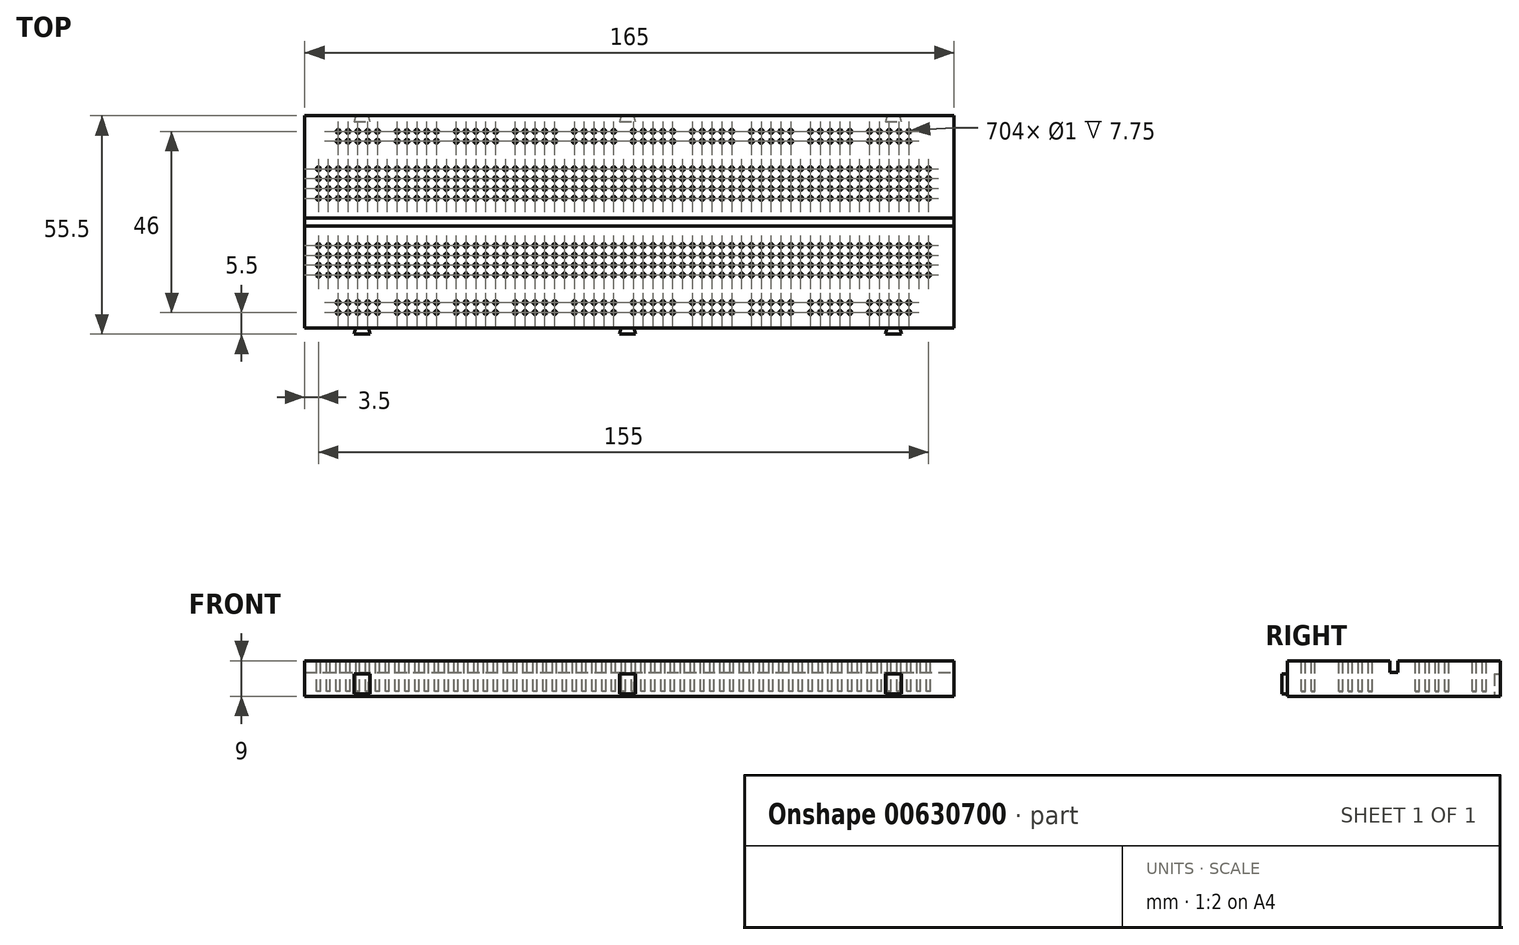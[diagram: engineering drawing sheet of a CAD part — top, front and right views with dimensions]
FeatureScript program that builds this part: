
annotation { "Feature Type Name" : "Feature", "Feature Type Description" : "" }
export const myFeature = defineFeature(function(context is Context, id is Id, definition is map)
    precondition{}
    {
        {
            var Q0;
            Q0=qCreatedBy(makeId("Top.planeOp"),FACE);
            var sketch = newSketch(context, id + "F0", { "sketchPlane" : qUnion([Q0])});
            skLineSegment(sketch, "E0.bottom", {"start": v(0, 0) * mm, "end": v(165, 0) * mm});
            skLineSegment(sketch, "E0.top", {"start": v(0, 54) * mm, "end": v(165, 54) * mm});
            skLineSegment(sketch, "E0.left", {"start": v(0, 0) * mm, "end": v(0, 54) * mm});
            skLineSegment(sketch, "E0.right", {"start": v(165, 0) * mm, "end": v(165, 54) * mm});
            skSolve(sketch);
        }
        {
            var Q0;
            Q0 = qSketchRegion(id + "F0", true);
            extrude(context, id + "F1", {"entities" : qUnion([Q0]), "depth" : 9 * mm, "offsetDistance" : 25 * mm});
        }
        {
            var Q0;
            Q0=makeQuery(id+"F1.opExtrude","CAP_FACE",FACE,{"disambiguationData":[OSD([sQuery(id+"F0.wireOp",EDGE,"E0.bottom"),sQuery(id+"F0.wireOp",EDGE,"E0.top"),sQuery(id+"F0.wireOp",EDGE,"E0.left"),sQuery(id+"F0.wireOp",EDGE,"E0.right")])],"isStart":false});
            var sketch = newSketch(context, id + "F2", { "sketchPlane" : qUnion([Q0])});
            skLineSegment(sketch, "E1.bottom", {"start": v(0, 28) * mm, "end": v(165, 28) * mm});
            skLineSegment(sketch, "E1.top", {"start": v(0, 26) * mm, "end": v(165, 26) * mm});
            skLineSegment(sketch, "E1.left", {"start": v(0, 28) * mm, "end": v(0, 26) * mm});
            skLineSegment(sketch, "E1.right", {"start": v(165, 28) * mm, "end": v(165, 26) * mm});
            skSolve(sketch);
        }
        {
            var Q0;
            Q0 = qSketchRegion(id + "F2", true);
            extrude(context, id + "F3", {"entities" : qUnion([Q0]), "operationType" : NewBodyOperationType.REMOVE, "oppositeDirection" : true, "depth" : 3 * mm, "offsetDistance" : 25 * mm});
        }
        {
            var Q0;
            {var subQ0=sQuery(id+"F0.wireOp",EDGE,"E0.top");var subQ1=sQuery(id+"F0.wireOp",EDGE,"E0.left");var subQ2=sQuery(id+"F0.wireOp",EDGE,"E0.right");Q0=makeQuery(id+"F3.boolean.opBoolean","SPLIT",FACE,{"disambiguationData":[TD([makeQuery(id+"F1.opExtrude","SWEPT_FACE",FACE,{"disambiguationData":[OSD([subQ0])]})])],"derivedFrom":makeQuery(id+"F1.opExtrude","CAP_FACE",FACE,{"disambiguationData":[OSD([sQuery(id+"F0.wireOp",EDGE,"E0.bottom"),subQ0,subQ1,subQ2])],"isStart":false})});}
            var sketch = newSketch(context, id + "F4", { "sketchPlane" : qUnion([Q0])});
            skCircle(sketch, "E2", {"center": v(3.5, 40.5) * mm, "radius": 0.5 * mm});
            skCircle(sketch, "E3", {"center": v(3.5, 38) * mm, "radius": 0.5 * mm});
            skCircle(sketch, "E4", {"center": v(3.5, 35.5) * mm, "radius": 0.5 * mm});
            skCircle(sketch, "E5", {"center": v(3.5, 33) * mm, "radius": 0.5 * mm});
            skCircle(sketch, "E6.1.0.0", {"center": v(6, 40.5) * mm, "radius": 0.5 * mm});
            skCircle(sketch, "E6.1.0.1", {"center": v(6, 38) * mm, "radius": 0.5 * mm});
            skCircle(sketch, "E6.1.0.2", {"center": v(6, 35.5) * mm, "radius": 0.5 * mm});
            skCircle(sketch, "E6.1.0.3", {"center": v(6, 33) * mm, "radius": 0.5 * mm});
            skCircle(sketch, "E6.2.0.0", {"center": v(8.5, 40.5) * mm, "radius": 0.5 * mm});
            skCircle(sketch, "E6.2.0.1", {"center": v(8.5, 38) * mm, "radius": 0.5 * mm});
            skCircle(sketch, "E6.2.0.2", {"center": v(8.5, 35.5) * mm, "radius": 0.5 * mm});
            skCircle(sketch, "E6.2.0.3", {"center": v(8.5, 33) * mm, "radius": 0.5 * mm});
            skCircle(sketch, "E6.3.0.0", {"center": v(11, 40.5) * mm, "radius": 0.5 * mm});
            skCircle(sketch, "E6.3.0.1", {"center": v(11, 38) * mm, "radius": 0.5 * mm});
            skCircle(sketch, "E6.3.0.2", {"center": v(11, 35.5) * mm, "radius": 0.5 * mm});
            skCircle(sketch, "E6.3.0.3", {"center": v(11, 33) * mm, "radius": 0.5 * mm});
            skCircle(sketch, "E6.4.0.0", {"center": v(13.5, 40.5) * mm, "radius": 0.5 * mm});
            skCircle(sketch, "E6.4.0.1", {"center": v(13.5, 38) * mm, "radius": 0.5 * mm});
            skCircle(sketch, "E6.4.0.2", {"center": v(13.5, 35.5) * mm, "radius": 0.5 * mm});
            skCircle(sketch, "E6.4.0.3", {"center": v(13.5, 33) * mm, "radius": 0.5 * mm});
            skCircle(sketch, "E6.5.0.0", {"center": v(16, 40.5) * mm, "radius": 0.5 * mm});
            skCircle(sketch, "E6.5.0.1", {"center": v(16, 38) * mm, "radius": 0.5 * mm});
            skCircle(sketch, "E6.5.0.2", {"center": v(16, 35.5) * mm, "radius": 0.5 * mm});
            skCircle(sketch, "E6.5.0.3", {"center": v(16, 33) * mm, "radius": 0.5 * mm});
            skCircle(sketch, "E6.6.0.0", {"center": v(18.5, 40.5) * mm, "radius": 0.5 * mm});
            skCircle(sketch, "E6.6.0.1", {"center": v(18.5, 38) * mm, "radius": 0.5 * mm});
            skCircle(sketch, "E6.6.0.2", {"center": v(18.5, 35.5) * mm, "radius": 0.5 * mm});
            skCircle(sketch, "E6.6.0.3", {"center": v(18.5, 33) * mm, "radius": 0.5 * mm});
            skCircle(sketch, "E6.7.0.0", {"center": v(21, 40.5) * mm, "radius": 0.5 * mm});
            skCircle(sketch, "E6.7.0.1", {"center": v(21, 38) * mm, "radius": 0.5 * mm});
            skCircle(sketch, "E6.7.0.2", {"center": v(21, 35.5) * mm, "radius": 0.5 * mm});
            skCircle(sketch, "E6.7.0.3", {"center": v(21, 33) * mm, "radius": 0.5 * mm});
            skCircle(sketch, "E6.8.0.0", {"center": v(23.5, 40.5) * mm, "radius": 0.5 * mm});
            skCircle(sketch, "E6.8.0.1", {"center": v(23.5, 38) * mm, "radius": 0.5 * mm});
            skCircle(sketch, "E6.8.0.2", {"center": v(23.5, 35.5) * mm, "radius": 0.5 * mm});
            skCircle(sketch, "E6.8.0.3", {"center": v(23.5, 33) * mm, "radius": 0.5 * mm});
            skCircle(sketch, "E6.9.0.0", {"center": v(26, 40.5) * mm, "radius": 0.5 * mm});
            skCircle(sketch, "E6.9.0.1", {"center": v(26, 38) * mm, "radius": 0.5 * mm});
            skCircle(sketch, "E6.9.0.2", {"center": v(26, 35.5) * mm, "radius": 0.5 * mm});
            skCircle(sketch, "E6.9.0.3", {"center": v(26, 33) * mm, "radius": 0.5 * mm});
            skCircle(sketch, "E6.10.0.0", {"center": v(28.5, 40.5) * mm, "radius": 0.5 * mm});
            skCircle(sketch, "E6.10.0.1", {"center": v(28.5, 38) * mm, "radius": 0.5 * mm});
            skCircle(sketch, "E6.10.0.2", {"center": v(28.5, 35.5) * mm, "radius": 0.5 * mm});
            skCircle(sketch, "E6.10.0.3", {"center": v(28.5, 33) * mm, "radius": 0.5 * mm});
            skCircle(sketch, "E6.11.0.0", {"center": v(31, 40.5) * mm, "radius": 0.5 * mm});
            skCircle(sketch, "E6.11.0.1", {"center": v(31, 38) * mm, "radius": 0.5 * mm});
            skCircle(sketch, "E6.11.0.2", {"center": v(31, 35.5) * mm, "radius": 0.5 * mm});
            skCircle(sketch, "E6.11.0.3", {"center": v(31, 33) * mm, "radius": 0.5 * mm});
            skCircle(sketch, "E6.12.0.0", {"center": v(33.5, 40.5) * mm, "radius": 0.5 * mm});
            skCircle(sketch, "E6.12.0.1", {"center": v(33.5, 38) * mm, "radius": 0.5 * mm});
            skCircle(sketch, "E6.12.0.2", {"center": v(33.5, 35.5) * mm, "radius": 0.5 * mm});
            skCircle(sketch, "E6.12.0.3", {"center": v(33.5, 33) * mm, "radius": 0.5 * mm});
            skCircle(sketch, "E6.13.0.0", {"center": v(36, 40.5) * mm, "radius": 0.5 * mm});
            skCircle(sketch, "E6.13.0.1", {"center": v(36, 38) * mm, "radius": 0.5 * mm});
            skCircle(sketch, "E6.13.0.2", {"center": v(36, 35.5) * mm, "radius": 0.5 * mm});
            skCircle(sketch, "E6.13.0.3", {"center": v(36, 33) * mm, "radius": 0.5 * mm});
            skCircle(sketch, "E6.14.0.0", {"center": v(38.5, 40.5) * mm, "radius": 0.5 * mm});
            skCircle(sketch, "E6.14.0.1", {"center": v(38.5, 38) * mm, "radius": 0.5 * mm});
            skCircle(sketch, "E6.14.0.2", {"center": v(38.5, 35.5) * mm, "radius": 0.5 * mm});
            skCircle(sketch, "E6.14.0.3", {"center": v(38.5, 33) * mm, "radius": 0.5 * mm});
            skCircle(sketch, "E6.15.0.0", {"center": v(41, 40.5) * mm, "radius": 0.5 * mm});
            skCircle(sketch, "E6.15.0.1", {"center": v(41, 38) * mm, "radius": 0.5 * mm});
            skCircle(sketch, "E6.15.0.2", {"center": v(41, 35.5) * mm, "radius": 0.5 * mm});
            skCircle(sketch, "E6.15.0.3", {"center": v(41, 33) * mm, "radius": 0.5 * mm});
            skCircle(sketch, "E6.16.0.0", {"center": v(43.5, 40.5) * mm, "radius": 0.5 * mm});
            skCircle(sketch, "E6.16.0.1", {"center": v(43.5, 38) * mm, "radius": 0.5 * mm});
            skCircle(sketch, "E6.16.0.2", {"center": v(43.5, 35.5) * mm, "radius": 0.5 * mm});
            skCircle(sketch, "E6.16.0.3", {"center": v(43.5, 33) * mm, "radius": 0.5 * mm});
            skCircle(sketch, "E6.17.0.0", {"center": v(46, 40.5) * mm, "radius": 0.5 * mm});
            skCircle(sketch, "E6.17.0.1", {"center": v(46, 38) * mm, "radius": 0.5 * mm});
            skCircle(sketch, "E6.17.0.2", {"center": v(46, 35.5) * mm, "radius": 0.5 * mm});
            skCircle(sketch, "E6.17.0.3", {"center": v(46, 33) * mm, "radius": 0.5 * mm});
            skCircle(sketch, "E6.18.0.0", {"center": v(48.5, 40.5) * mm, "radius": 0.5 * mm});
            skCircle(sketch, "E6.18.0.1", {"center": v(48.5, 38) * mm, "radius": 0.5 * mm});
            skCircle(sketch, "E6.18.0.2", {"center": v(48.5, 35.5) * mm, "radius": 0.5 * mm});
            skCircle(sketch, "E6.18.0.3", {"center": v(48.5, 33) * mm, "radius": 0.5 * mm});
            skCircle(sketch, "E6.19.0.0", {"center": v(51, 40.5) * mm, "radius": 0.5 * mm});
            skCircle(sketch, "E6.19.0.1", {"center": v(51, 38) * mm, "radius": 0.5 * mm});
            skCircle(sketch, "E6.19.0.2", {"center": v(51, 35.5) * mm, "radius": 0.5 * mm});
            skCircle(sketch, "E6.19.0.3", {"center": v(51, 33) * mm, "radius": 0.5 * mm});
            skCircle(sketch, "E6.20.0.0", {"center": v(53.5, 40.5) * mm, "radius": 0.5 * mm});
            skCircle(sketch, "E6.20.0.1", {"center": v(53.5, 38) * mm, "radius": 0.5 * mm});
            skCircle(sketch, "E6.20.0.2", {"center": v(53.5, 35.5) * mm, "radius": 0.5 * mm});
            skCircle(sketch, "E6.20.0.3", {"center": v(53.5, 33) * mm, "radius": 0.5 * mm});
            skCircle(sketch, "E6.21.0.0", {"center": v(56, 40.5) * mm, "radius": 0.5 * mm});
            skCircle(sketch, "E6.21.0.1", {"center": v(56, 38) * mm, "radius": 0.5 * mm});
            skCircle(sketch, "E6.21.0.2", {"center": v(56, 35.5) * mm, "radius": 0.5 * mm});
            skCircle(sketch, "E6.21.0.3", {"center": v(56, 33) * mm, "radius": 0.5 * mm});
            skCircle(sketch, "E6.22.0.0", {"center": v(58.5, 40.5) * mm, "radius": 0.5 * mm});
            skCircle(sketch, "E6.22.0.1", {"center": v(58.5, 38) * mm, "radius": 0.5 * mm});
            skCircle(sketch, "E6.22.0.2", {"center": v(58.5, 35.5) * mm, "radius": 0.5 * mm});
            skCircle(sketch, "E6.22.0.3", {"center": v(58.5, 33) * mm, "radius": 0.5 * mm});
            skCircle(sketch, "E6.23.0.0", {"center": v(61, 40.5) * mm, "radius": 0.5 * mm});
            skCircle(sketch, "E6.23.0.1", {"center": v(61, 38) * mm, "radius": 0.5 * mm});
            skCircle(sketch, "E6.23.0.2", {"center": v(61, 35.5) * mm, "radius": 0.5 * mm});
            skCircle(sketch, "E6.23.0.3", {"center": v(61, 33) * mm, "radius": 0.5 * mm});
            skCircle(sketch, "E6.24.0.0", {"center": v(63.5, 40.5) * mm, "radius": 0.5 * mm});
            skCircle(sketch, "E6.24.0.1", {"center": v(63.5, 38) * mm, "radius": 0.5 * mm});
            skCircle(sketch, "E6.24.0.2", {"center": v(63.5, 35.5) * mm, "radius": 0.5 * mm});
            skCircle(sketch, "E6.24.0.3", {"center": v(63.5, 33) * mm, "radius": 0.5 * mm});
            skCircle(sketch, "E6.25.0.0", {"center": v(66, 40.5) * mm, "radius": 0.5 * mm});
            skCircle(sketch, "E6.25.0.1", {"center": v(66, 38) * mm, "radius": 0.5 * mm});
            skCircle(sketch, "E6.25.0.2", {"center": v(66, 35.5) * mm, "radius": 0.5 * mm});
            skCircle(sketch, "E6.25.0.3", {"center": v(66, 33) * mm, "radius": 0.5 * mm});
            skCircle(sketch, "E6.26.0.0", {"center": v(68.5, 40.5) * mm, "radius": 0.5 * mm});
            skCircle(sketch, "E6.26.0.1", {"center": v(68.5, 38) * mm, "radius": 0.5 * mm});
            skCircle(sketch, "E6.26.0.2", {"center": v(68.5, 35.5) * mm, "radius": 0.5 * mm});
            skCircle(sketch, "E6.26.0.3", {"center": v(68.5, 33) * mm, "radius": 0.5 * mm});
            skCircle(sketch, "E6.27.0.0", {"center": v(71, 40.5) * mm, "radius": 0.5 * mm});
            skCircle(sketch, "E6.27.0.1", {"center": v(71, 38) * mm, "radius": 0.5 * mm});
            skCircle(sketch, "E6.27.0.2", {"center": v(71, 35.5) * mm, "radius": 0.5 * mm});
            skCircle(sketch, "E6.27.0.3", {"center": v(71, 33) * mm, "radius": 0.5 * mm});
            skCircle(sketch, "E6.28.0.0", {"center": v(73.5, 40.5) * mm, "radius": 0.5 * mm});
            skCircle(sketch, "E6.28.0.1", {"center": v(73.5, 38) * mm, "radius": 0.5 * mm});
            skCircle(sketch, "E6.28.0.2", {"center": v(73.5, 35.5) * mm, "radius": 0.5 * mm});
            skCircle(sketch, "E6.28.0.3", {"center": v(73.5, 33) * mm, "radius": 0.5 * mm});
            skCircle(sketch, "E6.29.0.0", {"center": v(76, 40.5) * mm, "radius": 0.5 * mm});
            skCircle(sketch, "E6.29.0.1", {"center": v(76, 38) * mm, "radius": 0.5 * mm});
            skCircle(sketch, "E6.29.0.2", {"center": v(76, 35.5) * mm, "radius": 0.5 * mm});
            skCircle(sketch, "E6.29.0.3", {"center": v(76, 33) * mm, "radius": 0.5 * mm});
            skCircle(sketch, "E6.30.0.0", {"center": v(78.5, 40.5) * mm, "radius": 0.5 * mm});
            skCircle(sketch, "E6.30.0.1", {"center": v(78.5, 38) * mm, "radius": 0.5 * mm});
            skCircle(sketch, "E6.30.0.2", {"center": v(78.5, 35.5) * mm, "radius": 0.5 * mm});
            skCircle(sketch, "E6.30.0.3", {"center": v(78.5, 33) * mm, "radius": 0.5 * mm});
            skCircle(sketch, "E6.31.0.0", {"center": v(81, 40.5) * mm, "radius": 0.5 * mm});
            skCircle(sketch, "E6.31.0.1", {"center": v(81, 38) * mm, "radius": 0.5 * mm});
            skCircle(sketch, "E6.31.0.2", {"center": v(81, 35.5) * mm, "radius": 0.5 * mm});
            skCircle(sketch, "E6.31.0.3", {"center": v(81, 33) * mm, "radius": 0.5 * mm});
            skCircle(sketch, "E6.32.0.0", {"center": v(83.5, 40.5) * mm, "radius": 0.5 * mm});
            skCircle(sketch, "E6.32.0.1", {"center": v(83.5, 38) * mm, "radius": 0.5 * mm});
            skCircle(sketch, "E6.32.0.2", {"center": v(83.5, 35.5) * mm, "radius": 0.5 * mm});
            skCircle(sketch, "E6.32.0.3", {"center": v(83.5, 33) * mm, "radius": 0.5 * mm});
            skCircle(sketch, "E6.33.0.0", {"center": v(86, 40.5) * mm, "radius": 0.5 * mm});
            skCircle(sketch, "E6.33.0.1", {"center": v(86, 38) * mm, "radius": 0.5 * mm});
            skCircle(sketch, "E6.33.0.2", {"center": v(86, 35.5) * mm, "radius": 0.5 * mm});
            skCircle(sketch, "E6.33.0.3", {"center": v(86, 33) * mm, "radius": 0.5 * mm});
            skCircle(sketch, "E6.34.0.0", {"center": v(88.5, 40.5) * mm, "radius": 0.5 * mm});
            skCircle(sketch, "E6.34.0.1", {"center": v(88.5, 38) * mm, "radius": 0.5 * mm});
            skCircle(sketch, "E6.34.0.2", {"center": v(88.5, 35.5) * mm, "radius": 0.5 * mm});
            skCircle(sketch, "E6.34.0.3", {"center": v(88.5, 33) * mm, "radius": 0.5 * mm});
            skCircle(sketch, "E6.35.0.0", {"center": v(91, 40.5) * mm, "radius": 0.5 * mm});
            skCircle(sketch, "E6.35.0.1", {"center": v(91, 38) * mm, "radius": 0.5 * mm});
            skCircle(sketch, "E6.35.0.2", {"center": v(91, 35.5) * mm, "radius": 0.5 * mm});
            skCircle(sketch, "E6.35.0.3", {"center": v(91, 33) * mm, "radius": 0.5 * mm});
            skCircle(sketch, "E6.36.0.0", {"center": v(93.5, 40.5) * mm, "radius": 0.5 * mm});
            skCircle(sketch, "E6.36.0.1", {"center": v(93.5, 38) * mm, "radius": 0.5 * mm});
            skCircle(sketch, "E6.36.0.2", {"center": v(93.5, 35.5) * mm, "radius": 0.5 * mm});
            skCircle(sketch, "E6.36.0.3", {"center": v(93.5, 33) * mm, "radius": 0.5 * mm});
            skCircle(sketch, "E6.37.0.0", {"center": v(96, 40.5) * mm, "radius": 0.5 * mm});
            skCircle(sketch, "E6.37.0.1", {"center": v(96, 38) * mm, "radius": 0.5 * mm});
            skCircle(sketch, "E6.37.0.2", {"center": v(96, 35.5) * mm, "radius": 0.5 * mm});
            skCircle(sketch, "E6.37.0.3", {"center": v(96, 33) * mm, "radius": 0.5 * mm});
            skCircle(sketch, "E6.38.0.0", {"center": v(98.5, 40.5) * mm, "radius": 0.5 * mm});
            skCircle(sketch, "E6.38.0.1", {"center": v(98.5, 38) * mm, "radius": 0.5 * mm});
            skCircle(sketch, "E6.38.0.2", {"center": v(98.5, 35.5) * mm, "radius": 0.5 * mm});
            skCircle(sketch, "E6.38.0.3", {"center": v(98.5, 33) * mm, "radius": 0.5 * mm});
            skCircle(sketch, "E6.39.0.0", {"center": v(101, 40.5) * mm, "radius": 0.5 * mm});
            skCircle(sketch, "E6.39.0.1", {"center": v(101, 38) * mm, "radius": 0.5 * mm});
            skCircle(sketch, "E6.39.0.2", {"center": v(101, 35.5) * mm, "radius": 0.5 * mm});
            skCircle(sketch, "E6.39.0.3", {"center": v(101, 33) * mm, "radius": 0.5 * mm});
            skCircle(sketch, "E6.40.0.0", {"center": v(103.5, 40.5) * mm, "radius": 0.5 * mm});
            skCircle(sketch, "E6.40.0.1", {"center": v(103.5, 38) * mm, "radius": 0.5 * mm});
            skCircle(sketch, "E6.40.0.2", {"center": v(103.5, 35.5) * mm, "radius": 0.5 * mm});
            skCircle(sketch, "E6.40.0.3", {"center": v(103.5, 33) * mm, "radius": 0.5 * mm});
            skCircle(sketch, "E6.41.0.0", {"center": v(106, 40.5) * mm, "radius": 0.5 * mm});
            skCircle(sketch, "E6.41.0.1", {"center": v(106, 38) * mm, "radius": 0.5 * mm});
            skCircle(sketch, "E6.41.0.2", {"center": v(106, 35.5) * mm, "radius": 0.5 * mm});
            skCircle(sketch, "E6.41.0.3", {"center": v(106, 33) * mm, "radius": 0.5 * mm});
            skCircle(sketch, "E6.42.0.0", {"center": v(108.5, 40.5) * mm, "radius": 0.5 * mm});
            skCircle(sketch, "E6.42.0.1", {"center": v(108.5, 38) * mm, "radius": 0.5 * mm});
            skCircle(sketch, "E6.42.0.2", {"center": v(108.5, 35.5) * mm, "radius": 0.5 * mm});
            skCircle(sketch, "E6.42.0.3", {"center": v(108.5, 33) * mm, "radius": 0.5 * mm});
            skCircle(sketch, "E6.43.0.0", {"center": v(111, 40.5) * mm, "radius": 0.5 * mm});
            skCircle(sketch, "E6.43.0.1", {"center": v(111, 38) * mm, "radius": 0.5 * mm});
            skCircle(sketch, "E6.43.0.2", {"center": v(111, 35.5) * mm, "radius": 0.5 * mm});
            skCircle(sketch, "E6.43.0.3", {"center": v(111, 33) * mm, "radius": 0.5 * mm});
            skCircle(sketch, "E6.44.0.0", {"center": v(113.5, 40.5) * mm, "radius": 0.5 * mm});
            skCircle(sketch, "E6.44.0.1", {"center": v(113.5, 38) * mm, "radius": 0.5 * mm});
            skCircle(sketch, "E6.44.0.2", {"center": v(113.5, 35.5) * mm, "radius": 0.5 * mm});
            skCircle(sketch, "E6.44.0.3", {"center": v(113.5, 33) * mm, "radius": 0.5 * mm});
            skCircle(sketch, "E6.45.0.0", {"center": v(116, 40.5) * mm, "radius": 0.5 * mm});
            skCircle(sketch, "E6.45.0.1", {"center": v(116, 38) * mm, "radius": 0.5 * mm});
            skCircle(sketch, "E6.45.0.2", {"center": v(116, 35.5) * mm, "radius": 0.5 * mm});
            skCircle(sketch, "E6.45.0.3", {"center": v(116, 33) * mm, "radius": 0.5 * mm});
            skCircle(sketch, "E6.46.0.0", {"center": v(118.5, 40.5) * mm, "radius": 0.5 * mm});
            skCircle(sketch, "E6.46.0.1", {"center": v(118.5, 38) * mm, "radius": 0.5 * mm});
            skCircle(sketch, "E6.46.0.2", {"center": v(118.5, 35.5) * mm, "radius": 0.5 * mm});
            skCircle(sketch, "E6.46.0.3", {"center": v(118.5, 33) * mm, "radius": 0.5 * mm});
            skCircle(sketch, "E6.47.0.0", {"center": v(121, 40.5) * mm, "radius": 0.5 * mm});
            skCircle(sketch, "E6.47.0.1", {"center": v(121, 38) * mm, "radius": 0.5 * mm});
            skCircle(sketch, "E6.47.0.2", {"center": v(121, 35.5) * mm, "radius": 0.5 * mm});
            skCircle(sketch, "E6.47.0.3", {"center": v(121, 33) * mm, "radius": 0.5 * mm});
            skCircle(sketch, "E6.48.0.0", {"center": v(123.5, 40.5) * mm, "radius": 0.5 * mm});
            skCircle(sketch, "E6.48.0.1", {"center": v(123.5, 38) * mm, "radius": 0.5 * mm});
            skCircle(sketch, "E6.48.0.2", {"center": v(123.5, 35.5) * mm, "radius": 0.5 * mm});
            skCircle(sketch, "E6.48.0.3", {"center": v(123.5, 33) * mm, "radius": 0.5 * mm});
            skCircle(sketch, "E6.49.0.0", {"center": v(126, 40.5) * mm, "radius": 0.5 * mm});
            skCircle(sketch, "E6.49.0.1", {"center": v(126, 38) * mm, "radius": 0.5 * mm});
            skCircle(sketch, "E6.49.0.2", {"center": v(126, 35.5) * mm, "radius": 0.5 * mm});
            skCircle(sketch, "E6.49.0.3", {"center": v(126, 33) * mm, "radius": 0.5 * mm});
            skCircle(sketch, "E6.50.0.0", {"center": v(128.5, 40.5) * mm, "radius": 0.5 * mm});
            skCircle(sketch, "E6.50.0.1", {"center": v(128.5, 38) * mm, "radius": 0.5 * mm});
            skCircle(sketch, "E6.50.0.2", {"center": v(128.5, 35.5) * mm, "radius": 0.5 * mm});
            skCircle(sketch, "E6.50.0.3", {"center": v(128.5, 33) * mm, "radius": 0.5 * mm});
            skCircle(sketch, "E6.51.0.0", {"center": v(131, 40.5) * mm, "radius": 0.5 * mm});
            skCircle(sketch, "E6.51.0.1", {"center": v(131, 38) * mm, "radius": 0.5 * mm});
            skCircle(sketch, "E6.51.0.2", {"center": v(131, 35.5) * mm, "radius": 0.5 * mm});
            skCircle(sketch, "E6.51.0.3", {"center": v(131, 33) * mm, "radius": 0.5 * mm});
            skCircle(sketch, "E6.52.0.0", {"center": v(133.5, 40.5) * mm, "radius": 0.5 * mm});
            skCircle(sketch, "E6.52.0.1", {"center": v(133.5, 38) * mm, "radius": 0.5 * mm});
            skCircle(sketch, "E6.52.0.2", {"center": v(133.5, 35.5) * mm, "radius": 0.5 * mm});
            skCircle(sketch, "E6.52.0.3", {"center": v(133.5, 33) * mm, "radius": 0.5 * mm});
            skCircle(sketch, "E6.53.0.0", {"center": v(136, 40.5) * mm, "radius": 0.5 * mm});
            skCircle(sketch, "E6.53.0.1", {"center": v(136, 38) * mm, "radius": 0.5 * mm});
            skCircle(sketch, "E6.53.0.2", {"center": v(136, 35.5) * mm, "radius": 0.5 * mm});
            skCircle(sketch, "E6.53.0.3", {"center": v(136, 33) * mm, "radius": 0.5 * mm});
            skCircle(sketch, "E6.54.0.0", {"center": v(138.5, 40.5) * mm, "radius": 0.5 * mm});
            skCircle(sketch, "E6.54.0.1", {"center": v(138.5, 38) * mm, "radius": 0.5 * mm});
            skCircle(sketch, "E6.54.0.2", {"center": v(138.5, 35.5) * mm, "radius": 0.5 * mm});
            skCircle(sketch, "E6.54.0.3", {"center": v(138.5, 33) * mm, "radius": 0.5 * mm});
            skCircle(sketch, "E6.55.0.0", {"center": v(141, 40.5) * mm, "radius": 0.5 * mm});
            skCircle(sketch, "E6.55.0.1", {"center": v(141, 38) * mm, "radius": 0.5 * mm});
            skCircle(sketch, "E6.55.0.2", {"center": v(141, 35.5) * mm, "radius": 0.5 * mm});
            skCircle(sketch, "E6.55.0.3", {"center": v(141, 33) * mm, "radius": 0.5 * mm});
            skCircle(sketch, "E6.56.0.0", {"center": v(143.5, 40.5) * mm, "radius": 0.5 * mm});
            skCircle(sketch, "E6.56.0.1", {"center": v(143.5, 38) * mm, "radius": 0.5 * mm});
            skCircle(sketch, "E6.56.0.2", {"center": v(143.5, 35.5) * mm, "radius": 0.5 * mm});
            skCircle(sketch, "E6.56.0.3", {"center": v(143.5, 33) * mm, "radius": 0.5 * mm});
            skCircle(sketch, "E6.57.0.0", {"center": v(146, 40.5) * mm, "radius": 0.5 * mm});
            skCircle(sketch, "E6.57.0.1", {"center": v(146, 38) * mm, "radius": 0.5 * mm});
            skCircle(sketch, "E6.57.0.2", {"center": v(146, 35.5) * mm, "radius": 0.5 * mm});
            skCircle(sketch, "E6.57.0.3", {"center": v(146, 33) * mm, "radius": 0.5 * mm});
            skCircle(sketch, "E6.58.0.0", {"center": v(148.5, 40.5) * mm, "radius": 0.5 * mm});
            skCircle(sketch, "E6.58.0.1", {"center": v(148.5, 38) * mm, "radius": 0.5 * mm});
            skCircle(sketch, "E6.58.0.2", {"center": v(148.5, 35.5) * mm, "radius": 0.5 * mm});
            skCircle(sketch, "E6.58.0.3", {"center": v(148.5, 33) * mm, "radius": 0.5 * mm});
            skCircle(sketch, "E6.59.0.0", {"center": v(151, 40.5) * mm, "radius": 0.5 * mm});
            skCircle(sketch, "E6.59.0.1", {"center": v(151, 38) * mm, "radius": 0.5 * mm});
            skCircle(sketch, "E6.59.0.2", {"center": v(151, 35.5) * mm, "radius": 0.5 * mm});
            skCircle(sketch, "E6.59.0.3", {"center": v(151, 33) * mm, "radius": 0.5 * mm});
            skCircle(sketch, "E6.60.0.0", {"center": v(153.5, 40.5) * mm, "radius": 0.5 * mm});
            skCircle(sketch, "E6.60.0.1", {"center": v(153.5, 38) * mm, "radius": 0.5 * mm});
            skCircle(sketch, "E6.60.0.2", {"center": v(153.5, 35.5) * mm, "radius": 0.5 * mm});
            skCircle(sketch, "E6.60.0.3", {"center": v(153.5, 33) * mm, "radius": 0.5 * mm});
            skCircle(sketch, "E6.61.0.0", {"center": v(156, 40.5) * mm, "radius": 0.5 * mm});
            skCircle(sketch, "E6.61.0.1", {"center": v(156, 38) * mm, "radius": 0.5 * mm});
            skCircle(sketch, "E6.61.0.2", {"center": v(156, 35.5) * mm, "radius": 0.5 * mm});
            skCircle(sketch, "E6.61.0.3", {"center": v(156, 33) * mm, "radius": 0.5 * mm});
            skCircle(sketch, "E6.62.0.0", {"center": v(158.5, 40.5) * mm, "radius": 0.5 * mm});
            skCircle(sketch, "E6.62.0.1", {"center": v(158.5, 38) * mm, "radius": 0.5 * mm});
            skCircle(sketch, "E6.62.0.2", {"center": v(158.5, 35.5) * mm, "radius": 0.5 * mm});
            skCircle(sketch, "E6.62.0.3", {"center": v(158.5, 33) * mm, "radius": 0.5 * mm});
            skLineSegment(sketch, "E6.direction1", {"start": v(3.5, 40.5) * mm, "end": v(6, 40.5) * mm, "construction": true});
            skLineSegment(sketch, "E7", {"start": v(171.18, 27) * mm, "end": v(-9.23, 27) * mm, "construction": true});
            skCircle(sketch, "E8", {"center": v(8.5, 47.5) * mm, "radius": 0.5 * mm});
            skCircle(sketch, "E9", {"center": v(8.5, 50) * mm, "radius": 0.5 * mm});
            skCircle(sketch, "E10.1.0.0", {"center": v(11, 50) * mm, "radius": 0.5 * mm});
            skCircle(sketch, "E10.1.0.1", {"center": v(11, 47.5) * mm, "radius": 0.5 * mm});
            skCircle(sketch, "E10.2.0.0", {"center": v(13.5, 50) * mm, "radius": 0.5 * mm});
            skCircle(sketch, "E10.2.0.1", {"center": v(13.5, 47.5) * mm, "radius": 0.5 * mm});
            skCircle(sketch, "E10.3.0.0", {"center": v(16, 50) * mm, "radius": 0.5 * mm});
            skCircle(sketch, "E10.3.0.1", {"center": v(16, 47.5) * mm, "radius": 0.5 * mm});
            skCircle(sketch, "E10.4.0.0", {"center": v(18.5, 50) * mm, "radius": 0.5 * mm});
            skCircle(sketch, "E10.4.0.1", {"center": v(18.5, 47.5) * mm, "radius": 0.5 * mm});
            skLineSegment(sketch, "E10.direction1", {"start": v(8.5, 50) * mm, "end": v(11, 50) * mm, "construction": true});
            skCircle(sketch, "E11.1.0.0", {"center": v(28.5, 50) * mm, "radius": 0.5 * mm});
            skCircle(sketch, "E11.1.0.1", {"center": v(26, 47.5) * mm, "radius": 0.5 * mm});
            skCircle(sketch, "E11.1.0.2", {"center": v(28.5, 47.5) * mm, "radius": 0.5 * mm});
            skCircle(sketch, "E11.1.0.3", {"center": v(26, 50) * mm, "radius": 0.5 * mm});
            skCircle(sketch, "E11.1.0.4", {"center": v(23.5, 50) * mm, "radius": 0.5 * mm});
            skCircle(sketch, "E11.1.0.5", {"center": v(31, 50) * mm, "radius": 0.5 * mm});
            skCircle(sketch, "E11.1.0.6", {"center": v(31, 47.5) * mm, "radius": 0.5 * mm});
            skCircle(sketch, "E11.1.0.7", {"center": v(33.5, 50) * mm, "radius": 0.5 * mm});
            skCircle(sketch, "E11.1.0.8", {"center": v(33.5, 47.5) * mm, "radius": 0.5 * mm});
            skLineSegment(sketch, "E11.1.0.9", {"start": v(23.5, 50) * mm, "end": v(26, 50) * mm, "construction": true});
            skCircle(sketch, "E11.1.0.10", {"center": v(23.5, 47.5) * mm, "radius": 0.5 * mm});
            skCircle(sketch, "E11.2.0.0", {"center": v(43.5, 50) * mm, "radius": 0.5 * mm});
            skCircle(sketch, "E11.2.0.1", {"center": v(41, 47.5) * mm, "radius": 0.5 * mm});
            skCircle(sketch, "E11.2.0.2", {"center": v(43.5, 47.5) * mm, "radius": 0.5 * mm});
            skCircle(sketch, "E11.2.0.3", {"center": v(41, 50) * mm, "radius": 0.5 * mm});
            skCircle(sketch, "E11.2.0.4", {"center": v(38.5, 50) * mm, "radius": 0.5 * mm});
            skCircle(sketch, "E11.2.0.5", {"center": v(46, 50) * mm, "radius": 0.5 * mm});
            skCircle(sketch, "E11.2.0.6", {"center": v(46, 47.5) * mm, "radius": 0.5 * mm});
            skCircle(sketch, "E11.2.0.7", {"center": v(48.5, 50) * mm, "radius": 0.5 * mm});
            skCircle(sketch, "E11.2.0.8", {"center": v(48.5, 47.5) * mm, "radius": 0.5 * mm});
            skLineSegment(sketch, "E11.2.0.9", {"start": v(38.5, 50) * mm, "end": v(41, 50) * mm, "construction": true});
            skCircle(sketch, "E11.2.0.10", {"center": v(38.5, 47.5) * mm, "radius": 0.5 * mm});
            skCircle(sketch, "E11.3.0.0", {"center": v(58.5, 50) * mm, "radius": 0.5 * mm});
            skCircle(sketch, "E11.3.0.1", {"center": v(56, 47.5) * mm, "radius": 0.5 * mm});
            skCircle(sketch, "E11.3.0.2", {"center": v(58.5, 47.5) * mm, "radius": 0.5 * mm});
            skCircle(sketch, "E11.3.0.3", {"center": v(56, 50) * mm, "radius": 0.5 * mm});
            skCircle(sketch, "E11.3.0.4", {"center": v(53.5, 50) * mm, "radius": 0.5 * mm});
            skCircle(sketch, "E11.3.0.5", {"center": v(61, 50) * mm, "radius": 0.5 * mm});
            skCircle(sketch, "E11.3.0.6", {"center": v(61, 47.5) * mm, "radius": 0.5 * mm});
            skCircle(sketch, "E11.3.0.7", {"center": v(63.5, 50) * mm, "radius": 0.5 * mm});
            skCircle(sketch, "E11.3.0.8", {"center": v(63.5, 47.5) * mm, "radius": 0.5 * mm});
            skLineSegment(sketch, "E11.3.0.9", {"start": v(53.5, 50) * mm, "end": v(56, 50) * mm, "construction": true});
            skCircle(sketch, "E11.3.0.10", {"center": v(53.5, 47.5) * mm, "radius": 0.5 * mm});
            skCircle(sketch, "E11.4.0.0", {"center": v(73.5, 50) * mm, "radius": 0.5 * mm});
            skCircle(sketch, "E11.4.0.1", {"center": v(71, 47.5) * mm, "radius": 0.5 * mm});
            skCircle(sketch, "E11.4.0.2", {"center": v(73.5, 47.5) * mm, "radius": 0.5 * mm});
            skCircle(sketch, "E11.4.0.3", {"center": v(71, 50) * mm, "radius": 0.5 * mm});
            skCircle(sketch, "E11.4.0.4", {"center": v(68.5, 50) * mm, "radius": 0.5 * mm});
            skCircle(sketch, "E11.4.0.5", {"center": v(76, 50) * mm, "radius": 0.5 * mm});
            skCircle(sketch, "E11.4.0.6", {"center": v(76, 47.5) * mm, "radius": 0.5 * mm});
            skCircle(sketch, "E11.4.0.7", {"center": v(78.5, 50) * mm, "radius": 0.5 * mm});
            skCircle(sketch, "E11.4.0.8", {"center": v(78.5, 47.5) * mm, "radius": 0.5 * mm});
            skLineSegment(sketch, "E11.4.0.9", {"start": v(68.5, 50) * mm, "end": v(71, 50) * mm, "construction": true});
            skCircle(sketch, "E11.4.0.10", {"center": v(68.5, 47.5) * mm, "radius": 0.5 * mm});
            skCircle(sketch, "E11.5.0.0", {"center": v(88.5, 50) * mm, "radius": 0.5 * mm});
            skCircle(sketch, "E11.5.0.1", {"center": v(86, 47.5) * mm, "radius": 0.5 * mm});
            skCircle(sketch, "E11.5.0.2", {"center": v(88.5, 47.5) * mm, "radius": 0.5 * mm});
            skCircle(sketch, "E11.5.0.3", {"center": v(86, 50) * mm, "radius": 0.5 * mm});
            skCircle(sketch, "E11.5.0.4", {"center": v(83.5, 50) * mm, "radius": 0.5 * mm});
            skCircle(sketch, "E11.5.0.5", {"center": v(91, 50) * mm, "radius": 0.5 * mm});
            skCircle(sketch, "E11.5.0.6", {"center": v(91, 47.5) * mm, "radius": 0.5 * mm});
            skCircle(sketch, "E11.5.0.7", {"center": v(93.5, 50) * mm, "radius": 0.5 * mm});
            skCircle(sketch, "E11.5.0.8", {"center": v(93.5, 47.5) * mm, "radius": 0.5 * mm});
            skLineSegment(sketch, "E11.5.0.9", {"start": v(83.5, 50) * mm, "end": v(86, 50) * mm, "construction": true});
            skCircle(sketch, "E11.5.0.10", {"center": v(83.5, 47.5) * mm, "radius": 0.5 * mm});
            skCircle(sketch, "E11.6.0.0", {"center": v(103.5, 50) * mm, "radius": 0.5 * mm});
            skCircle(sketch, "E11.6.0.1", {"center": v(101, 47.5) * mm, "radius": 0.5 * mm});
            skCircle(sketch, "E11.6.0.2", {"center": v(103.5, 47.5) * mm, "radius": 0.5 * mm});
            skCircle(sketch, "E11.6.0.3", {"center": v(101, 50) * mm, "radius": 0.5 * mm});
            skCircle(sketch, "E11.6.0.4", {"center": v(98.5, 50) * mm, "radius": 0.5 * mm});
            skCircle(sketch, "E11.6.0.5", {"center": v(106, 50) * mm, "radius": 0.5 * mm});
            skCircle(sketch, "E11.6.0.6", {"center": v(106, 47.5) * mm, "radius": 0.5 * mm});
            skCircle(sketch, "E11.6.0.7", {"center": v(108.5, 50) * mm, "radius": 0.5 * mm});
            skCircle(sketch, "E11.6.0.8", {"center": v(108.5, 47.5) * mm, "radius": 0.5 * mm});
            skLineSegment(sketch, "E11.6.0.9", {"start": v(98.5, 50) * mm, "end": v(101, 50) * mm, "construction": true});
            skCircle(sketch, "E11.6.0.10", {"center": v(98.5, 47.5) * mm, "radius": 0.5 * mm});
            skCircle(sketch, "E11.7.0.0", {"center": v(118.5, 50) * mm, "radius": 0.5 * mm});
            skCircle(sketch, "E11.7.0.1", {"center": v(116, 47.5) * mm, "radius": 0.5 * mm});
            skCircle(sketch, "E11.7.0.2", {"center": v(118.5, 47.5) * mm, "radius": 0.5 * mm});
            skCircle(sketch, "E11.7.0.3", {"center": v(116, 50) * mm, "radius": 0.5 * mm});
            skCircle(sketch, "E11.7.0.4", {"center": v(113.5, 50) * mm, "radius": 0.5 * mm});
            skCircle(sketch, "E11.7.0.5", {"center": v(121, 50) * mm, "radius": 0.5 * mm});
            skCircle(sketch, "E11.7.0.6", {"center": v(121, 47.5) * mm, "radius": 0.5 * mm});
            skCircle(sketch, "E11.7.0.7", {"center": v(123.5, 50) * mm, "radius": 0.5 * mm});
            skCircle(sketch, "E11.7.0.8", {"center": v(123.5, 47.5) * mm, "radius": 0.5 * mm});
            skLineSegment(sketch, "E11.7.0.9", {"start": v(113.5, 50) * mm, "end": v(116, 50) * mm, "construction": true});
            skCircle(sketch, "E11.7.0.10", {"center": v(113.5, 47.5) * mm, "radius": 0.5 * mm});
            skCircle(sketch, "E11.8.0.0", {"center": v(133.5, 50) * mm, "radius": 0.5 * mm});
            skCircle(sketch, "E11.8.0.1", {"center": v(131, 47.5) * mm, "radius": 0.5 * mm});
            skCircle(sketch, "E11.8.0.2", {"center": v(133.5, 47.5) * mm, "radius": 0.5 * mm});
            skCircle(sketch, "E11.8.0.3", {"center": v(131, 50) * mm, "radius": 0.5 * mm});
            skCircle(sketch, "E11.8.0.4", {"center": v(128.5, 50) * mm, "radius": 0.5 * mm});
            skCircle(sketch, "E11.8.0.5", {"center": v(136, 50) * mm, "radius": 0.5 * mm});
            skCircle(sketch, "E11.8.0.6", {"center": v(136, 47.5) * mm, "radius": 0.5 * mm});
            skCircle(sketch, "E11.8.0.7", {"center": v(138.5, 50) * mm, "radius": 0.5 * mm});
            skCircle(sketch, "E11.8.0.8", {"center": v(138.5, 47.5) * mm, "radius": 0.5 * mm});
            skLineSegment(sketch, "E11.8.0.9", {"start": v(128.5, 50) * mm, "end": v(131, 50) * mm, "construction": true});
            skCircle(sketch, "E11.8.0.10", {"center": v(128.5, 47.5) * mm, "radius": 0.5 * mm});
            skCircle(sketch, "E11.9.0.0", {"center": v(148.5, 50) * mm, "radius": 0.5 * mm});
            skCircle(sketch, "E11.9.0.1", {"center": v(146, 47.5) * mm, "radius": 0.5 * mm});
            skCircle(sketch, "E11.9.0.2", {"center": v(148.5, 47.5) * mm, "radius": 0.5 * mm});
            skCircle(sketch, "E11.9.0.3", {"center": v(146, 50) * mm, "radius": 0.5 * mm});
            skCircle(sketch, "E11.9.0.4", {"center": v(143.5, 50) * mm, "radius": 0.5 * mm});
            skCircle(sketch, "E11.9.0.5", {"center": v(151, 50) * mm, "radius": 0.5 * mm});
            skCircle(sketch, "E11.9.0.6", {"center": v(151, 47.5) * mm, "radius": 0.5 * mm});
            skCircle(sketch, "E11.9.0.7", {"center": v(153.5, 50) * mm, "radius": 0.5 * mm});
            skCircle(sketch, "E11.9.0.8", {"center": v(153.5, 47.5) * mm, "radius": 0.5 * mm});
            skLineSegment(sketch, "E11.9.0.9", {"start": v(143.5, 50) * mm, "end": v(146, 50) * mm, "construction": true});
            skCircle(sketch, "E11.9.0.10", {"center": v(143.5, 47.5) * mm, "radius": 0.5 * mm});
            skLineSegment(sketch, "E11.direction1", {"start": v(8.5, 47.5) * mm, "end": v(23.5, 47.5) * mm, "construction": true});
            skCircle(sketch, "E12.MirrorC", {"center": v(8.5, 6.5) * mm, "radius": 0.5 * mm});
            skCircle(sketch, "E13.MirrorC", {"center": v(68.5, 4) * mm, "radius": 0.5 * mm});
            skLineSegment(sketch, "E14.MirrorCS", {"start": v(83.5, 4) * mm, "end": v(86, 4) * mm, "construction": true});
            skCircle(sketch, "E15.MirrorC", {"center": v(6, 13.5) * mm, "radius": 0.5 * mm});
            skCircle(sketch, "E16.MirrorC", {"center": v(3.5, 13.5) * mm, "radius": 0.5 * mm});
            skCircle(sketch, "E17.MirrorC", {"center": v(71, 4) * mm, "radius": 0.5 * mm});
            skCircle(sketch, "E18.MirrorC", {"center": v(23.5, 4) * mm, "radius": 0.5 * mm});
            skLineSegment(sketch, "E19.MirrorCS", {"start": v(38.5, 4) * mm, "end": v(41, 4) * mm, "construction": true});
            skCircle(sketch, "E20.MirrorC", {"center": v(8.5, 4) * mm, "radius": 0.5 * mm});
            skLineSegment(sketch, "E21.MirrorCS", {"start": v(128.5, 4) * mm, "end": v(131, 4) * mm, "construction": true});
            skCircle(sketch, "E22.MirrorC", {"center": v(11, 4) * mm, "radius": 0.5 * mm});
            skCircle(sketch, "E23.MirrorC", {"center": v(146, 4) * mm, "radius": 0.5 * mm});
            skCircle(sketch, "E24.MirrorC", {"center": v(143.5, 4) * mm, "radius": 0.5 * mm});
            skCircle(sketch, "E25.MirrorC", {"center": v(56, 4) * mm, "radius": 0.5 * mm});
            skLineSegment(sketch, "E26.MirrorCS", {"start": v(23.5, 4) * mm, "end": v(26, 4) * mm, "construction": true});
            skCircle(sketch, "E27.MirrorC", {"center": v(41, 4) * mm, "radius": 0.5 * mm});
            skLineSegment(sketch, "E28.MirrorCS", {"start": v(8.5, 4) * mm, "end": v(11, 4) * mm, "construction": true});
            skLineSegment(sketch, "E29.MirrorCS", {"start": v(53.5, 4) * mm, "end": v(56, 4) * mm, "construction": true});
            skCircle(sketch, "E30.MirrorC", {"center": v(38.5, 4) * mm, "radius": 0.5 * mm});
            skCircle(sketch, "E31.MirrorC", {"center": v(83.5, 4) * mm, "radius": 0.5 * mm});
            skCircle(sketch, "E32.MirrorC", {"center": v(131, 4) * mm, "radius": 0.5 * mm});
            skLineSegment(sketch, "E33.MirrorCS", {"start": v(3.5, 13.5) * mm, "end": v(6, 13.5) * mm, "construction": true});
            skCircle(sketch, "E34.MirrorC", {"center": v(26, 4) * mm, "radius": 0.5 * mm});
            skLineSegment(sketch, "E35.MirrorCS", {"start": v(68.5, 4) * mm, "end": v(71, 4) * mm, "construction": true});
            skLineSegment(sketch, "E36.MirrorCS", {"start": v(143.5, 4) * mm, "end": v(146, 4) * mm, "construction": true});
            skCircle(sketch, "E37.MirrorC", {"center": v(128.5, 4) * mm, "radius": 0.5 * mm});
            skCircle(sketch, "E38.MirrorC", {"center": v(23.5, 6.5) * mm, "radius": 0.5 * mm});
            skCircle(sketch, "E39.MirrorC", {"center": v(53.5, 4) * mm, "radius": 0.5 * mm});
            skCircle(sketch, "E40.MirrorC", {"center": v(151, 18.5) * mm, "radius": 0.5 * mm});
            skCircle(sketch, "E41.MirrorC", {"center": v(31, 4) * mm, "radius": 0.5 * mm});
            skCircle(sketch, "E42.MirrorC", {"center": v(38.5, 6.5) * mm, "radius": 0.5 * mm});
            skCircle(sketch, "E43.MirrorC", {"center": v(111, 18.5) * mm, "radius": 0.5 * mm});
            skCircle(sketch, "E44.MirrorC", {"center": v(121, 18.5) * mm, "radius": 0.5 * mm});
            skCircle(sketch, "E45.MirrorC", {"center": v(131, 18.5) * mm, "radius": 0.5 * mm});
            skCircle(sketch, "E46.MirrorC", {"center": v(141, 18.5) * mm, "radius": 0.5 * mm});
            skCircle(sketch, "E47.MirrorC", {"center": v(71, 18.5) * mm, "radius": 0.5 * mm});
            skCircle(sketch, "E48.MirrorC", {"center": v(81, 18.5) * mm, "radius": 0.5 * mm});
            skCircle(sketch, "E49.MirrorC", {"center": v(91, 18.5) * mm, "radius": 0.5 * mm});
            skCircle(sketch, "E50.MirrorC", {"center": v(101, 18.5) * mm, "radius": 0.5 * mm});
            skCircle(sketch, "E51.MirrorC", {"center": v(31, 18.5) * mm, "radius": 0.5 * mm});
            skCircle(sketch, "E52.MirrorC", {"center": v(41, 18.5) * mm, "radius": 0.5 * mm});
            skCircle(sketch, "E53.MirrorC", {"center": v(51, 18.5) * mm, "radius": 0.5 * mm});
            skCircle(sketch, "E54.MirrorC", {"center": v(61, 18.5) * mm, "radius": 0.5 * mm});
            skCircle(sketch, "E55.MirrorC", {"center": v(21, 18.5) * mm, "radius": 0.5 * mm});
            skCircle(sketch, "E56.MirrorC", {"center": v(11, 13.5) * mm, "radius": 0.5 * mm});
            skCircle(sketch, "E57.MirrorC", {"center": v(8.5, 21) * mm, "radius": 0.5 * mm});
            skCircle(sketch, "E58.MirrorC", {"center": v(8.5, 18.5) * mm, "radius": 0.5 * mm});
            skCircle(sketch, "E59.MirrorC", {"center": v(8.5, 16) * mm, "radius": 0.5 * mm});
            skCircle(sketch, "E60.MirrorC", {"center": v(8.5, 13.5) * mm, "radius": 0.5 * mm});
            skCircle(sketch, "E61.MirrorC", {"center": v(138.5, 6.5) * mm, "radius": 0.5 * mm});
            skCircle(sketch, "E62.MirrorC", {"center": v(6, 21) * mm, "radius": 0.5 * mm});
            skCircle(sketch, "E63.MirrorC", {"center": v(6, 18.5) * mm, "radius": 0.5 * mm});
            skCircle(sketch, "E64.MirrorC", {"center": v(6, 16) * mm, "radius": 0.5 * mm});
            skCircle(sketch, "E65.MirrorC", {"center": v(3.5, 21) * mm, "radius": 0.5 * mm});
            skCircle(sketch, "E66.MirrorC", {"center": v(3.5, 18.5) * mm, "radius": 0.5 * mm});
            skCircle(sketch, "E67.MirrorC", {"center": v(3.5, 16) * mm, "radius": 0.5 * mm});
            skCircle(sketch, "E68.MirrorC", {"center": v(11, 21) * mm, "radius": 0.5 * mm});
            skCircle(sketch, "E69.MirrorC", {"center": v(11, 18.5) * mm, "radius": 0.5 * mm});
            skCircle(sketch, "E70.MirrorC", {"center": v(11, 16) * mm, "radius": 0.5 * mm});
            skCircle(sketch, "E71.MirrorC", {"center": v(111, 16) * mm, "radius": 0.5 * mm});
            skCircle(sketch, "E72.MirrorC", {"center": v(121, 16) * mm, "radius": 0.5 * mm});
            skCircle(sketch, "E73.MirrorC", {"center": v(141, 16) * mm, "radius": 0.5 * mm});
            skCircle(sketch, "E74.MirrorC", {"center": v(131, 16) * mm, "radius": 0.5 * mm});
            skCircle(sketch, "E75.MirrorC", {"center": v(71, 16) * mm, "radius": 0.5 * mm});
            skCircle(sketch, "E76.MirrorC", {"center": v(81, 16) * mm, "radius": 0.5 * mm});
            skCircle(sketch, "E77.MirrorC", {"center": v(91, 16) * mm, "radius": 0.5 * mm});
            skCircle(sketch, "E78.MirrorC", {"center": v(101, 16) * mm, "radius": 0.5 * mm});
            skCircle(sketch, "E79.MirrorC", {"center": v(31, 16) * mm, "radius": 0.5 * mm});
            skCircle(sketch, "E80.MirrorC", {"center": v(41, 16) * mm, "radius": 0.5 * mm});
            skCircle(sketch, "E81.MirrorC", {"center": v(51, 16) * mm, "radius": 0.5 * mm});
            skCircle(sketch, "E82.MirrorC", {"center": v(61, 16) * mm, "radius": 0.5 * mm});
            skCircle(sketch, "E83.MirrorC", {"center": v(21, 16) * mm, "radius": 0.5 * mm});
            skCircle(sketch, "E84.MirrorC", {"center": v(138.5, 4) * mm, "radius": 0.5 * mm});
            skCircle(sketch, "E85.MirrorC", {"center": v(151, 16) * mm, "radius": 0.5 * mm});
            skCircle(sketch, "E86.MirrorC", {"center": v(136, 6.5) * mm, "radius": 0.5 * mm});
            skCircle(sketch, "E87.MirrorC", {"center": v(21, 21) * mm, "radius": 0.5 * mm});
            skCircle(sketch, "E88.MirrorC", {"center": v(61, 21) * mm, "radius": 0.5 * mm});
            skCircle(sketch, "E89.MirrorC", {"center": v(51, 21) * mm, "radius": 0.5 * mm});
            skCircle(sketch, "E90.MirrorC", {"center": v(41, 21) * mm, "radius": 0.5 * mm});
            skCircle(sketch, "E91.MirrorC", {"center": v(31, 21) * mm, "radius": 0.5 * mm});
            skCircle(sketch, "E92.MirrorC", {"center": v(101, 21) * mm, "radius": 0.5 * mm});
            skCircle(sketch, "E93.MirrorC", {"center": v(91, 21) * mm, "radius": 0.5 * mm});
            skCircle(sketch, "E94.MirrorC", {"center": v(81, 21) * mm, "radius": 0.5 * mm});
            skCircle(sketch, "E95.MirrorC", {"center": v(71, 21) * mm, "radius": 0.5 * mm});
            skCircle(sketch, "E96.MirrorC", {"center": v(141, 21) * mm, "radius": 0.5 * mm});
            skCircle(sketch, "E97.MirrorC", {"center": v(131, 21) * mm, "radius": 0.5 * mm});
            skCircle(sketch, "E98.MirrorC", {"center": v(121, 21) * mm, "radius": 0.5 * mm});
            skCircle(sketch, "E99.MirrorC", {"center": v(111, 21) * mm, "radius": 0.5 * mm});
            skCircle(sketch, "E100.MirrorC", {"center": v(58.5, 4) * mm, "radius": 0.5 * mm});
            skCircle(sketch, "E101.MirrorC", {"center": v(31, 6.5) * mm, "radius": 0.5 * mm});
            skCircle(sketch, "E102.MirrorC", {"center": v(151, 21) * mm, "radius": 0.5 * mm});
            skCircle(sketch, "E103.MirrorC", {"center": v(76, 4) * mm, "radius": 0.5 * mm});
            skCircle(sketch, "E104.MirrorC", {"center": v(83.5, 6.5) * mm, "radius": 0.5 * mm});
            skCircle(sketch, "E105.MirrorC", {"center": v(23.5, 13.5) * mm, "radius": 0.5 * mm});
            skCircle(sketch, "E106.MirrorC", {"center": v(13.5, 13.5) * mm, "radius": 0.5 * mm});
            skCircle(sketch, "E107.MirrorC", {"center": v(63.5, 13.5) * mm, "radius": 0.5 * mm});
            skCircle(sketch, "E108.MirrorC", {"center": v(43.5, 13.5) * mm, "radius": 0.5 * mm});
            skCircle(sketch, "E109.MirrorC", {"center": v(53.5, 13.5) * mm, "radius": 0.5 * mm});
            skCircle(sketch, "E110.MirrorC", {"center": v(103.5, 13.5) * mm, "radius": 0.5 * mm});
            skCircle(sketch, "E111.MirrorC", {"center": v(33.5, 13.5) * mm, "radius": 0.5 * mm});
            skCircle(sketch, "E112.MirrorC", {"center": v(93.5, 13.5) * mm, "radius": 0.5 * mm});
            skCircle(sketch, "E113.MirrorC", {"center": v(83.5, 13.5) * mm, "radius": 0.5 * mm});
            skCircle(sketch, "E114.MirrorC", {"center": v(73.5, 13.5) * mm, "radius": 0.5 * mm});
            skCircle(sketch, "E115.MirrorC", {"center": v(143.5, 13.5) * mm, "radius": 0.5 * mm});
            skCircle(sketch, "E116.MirrorC", {"center": v(133.5, 13.5) * mm, "radius": 0.5 * mm});
            skCircle(sketch, "E117.MirrorC", {"center": v(123.5, 13.5) * mm, "radius": 0.5 * mm});
            skCircle(sketch, "E118.MirrorC", {"center": v(113.5, 13.5) * mm, "radius": 0.5 * mm});
            skCircle(sketch, "E119.MirrorC", {"center": v(56, 6.5) * mm, "radius": 0.5 * mm});
            skCircle(sketch, "E120.MirrorC", {"center": v(33.5, 4) * mm, "radius": 0.5 * mm});
            skCircle(sketch, "E121.MirrorC", {"center": v(153.5, 13.5) * mm, "radius": 0.5 * mm});
            skCircle(sketch, "E122.MirrorC", {"center": v(128.5, 6.5) * mm, "radius": 0.5 * mm});
            skCircle(sketch, "E123.MirrorC", {"center": v(16, 4) * mm, "radius": 0.5 * mm});
            skCircle(sketch, "E124.MirrorC", {"center": v(156, 13.5) * mm, "radius": 0.5 * mm});
            skCircle(sketch, "E125.MirrorC", {"center": v(76, 6.5) * mm, "radius": 0.5 * mm});
            skCircle(sketch, "E126.MirrorC", {"center": v(68.5, 6.5) * mm, "radius": 0.5 * mm});
            skCircle(sketch, "E127.MirrorC", {"center": v(26, 13.5) * mm, "radius": 0.5 * mm});
            skCircle(sketch, "E128.MirrorC", {"center": v(16, 13.5) * mm, "radius": 0.5 * mm});
            skCircle(sketch, "E129.MirrorC", {"center": v(66, 13.5) * mm, "radius": 0.5 * mm});
            skCircle(sketch, "E130.MirrorC", {"center": v(56, 13.5) * mm, "radius": 0.5 * mm});
            skCircle(sketch, "E131.MirrorC", {"center": v(63.5, 16) * mm, "radius": 0.5 * mm});
            skCircle(sketch, "E132.MirrorC", {"center": v(46, 13.5) * mm, "radius": 0.5 * mm});
            skCircle(sketch, "E133.MirrorC", {"center": v(36, 13.5) * mm, "radius": 0.5 * mm});
            skCircle(sketch, "E134.MirrorC", {"center": v(53.5, 16) * mm, "radius": 0.5 * mm});
            skCircle(sketch, "E135.MirrorC", {"center": v(43.5, 16) * mm, "radius": 0.5 * mm});
            skCircle(sketch, "E136.MirrorC", {"center": v(33.5, 16) * mm, "radius": 0.5 * mm});
            skCircle(sketch, "E137.MirrorC", {"center": v(103.5, 16) * mm, "radius": 0.5 * mm});
            skCircle(sketch, "E138.MirrorC", {"center": v(93.5, 16) * mm, "radius": 0.5 * mm});
            skCircle(sketch, "E139.MirrorC", {"center": v(73.5, 16) * mm, "radius": 0.5 * mm});
            skCircle(sketch, "E140.MirrorC", {"center": v(83.5, 16) * mm, "radius": 0.5 * mm});
            skCircle(sketch, "E141.MirrorC", {"center": v(143.5, 16) * mm, "radius": 0.5 * mm});
            skCircle(sketch, "E142.MirrorC", {"center": v(133.5, 16) * mm, "radius": 0.5 * mm});
            skCircle(sketch, "E143.MirrorC", {"center": v(113.5, 16) * mm, "radius": 0.5 * mm});
            skCircle(sketch, "E144.MirrorC", {"center": v(123.5, 16) * mm, "radius": 0.5 * mm});
            skCircle(sketch, "E145.MirrorC", {"center": v(33.5, 6.5) * mm, "radius": 0.5 * mm});
            skCircle(sketch, "E146.MirrorC", {"center": v(58.5, 6.5) * mm, "radius": 0.5 * mm});
            skCircle(sketch, "E147.MirrorC", {"center": v(11, 6.5) * mm, "radius": 0.5 * mm});
            skCircle(sketch, "E148.MirrorC", {"center": v(153.5, 16) * mm, "radius": 0.5 * mm});
            skCircle(sketch, "E149.MirrorC", {"center": v(148.5, 4) * mm, "radius": 0.5 * mm});
            skCircle(sketch, "E150.MirrorC", {"center": v(78.5, 4) * mm, "radius": 0.5 * mm});
            skCircle(sketch, "E151.MirrorC", {"center": v(106, 13.5) * mm, "radius": 0.5 * mm});
            skCircle(sketch, "E152.MirrorC", {"center": v(96, 13.5) * mm, "radius": 0.5 * mm});
            skCircle(sketch, "E153.MirrorC", {"center": v(86, 13.5) * mm, "radius": 0.5 * mm});
            skCircle(sketch, "E154.MirrorC", {"center": v(76, 13.5) * mm, "radius": 0.5 * mm});
            skCircle(sketch, "E155.MirrorC", {"center": v(146, 13.5) * mm, "radius": 0.5 * mm});
            skCircle(sketch, "E156.MirrorC", {"center": v(136, 13.5) * mm, "radius": 0.5 * mm});
            skCircle(sketch, "E157.MirrorC", {"center": v(126, 13.5) * mm, "radius": 0.5 * mm});
            skCircle(sketch, "E158.MirrorC", {"center": v(116, 13.5) * mm, "radius": 0.5 * mm});
            skCircle(sketch, "E159.MirrorC", {"center": v(23.5, 16) * mm, "radius": 0.5 * mm});
            skCircle(sketch, "E160.MirrorC", {"center": v(13.5, 16) * mm, "radius": 0.5 * mm});
            skCircle(sketch, "E161.MirrorC", {"center": v(103.5, 18.5) * mm, "radius": 0.5 * mm});
            skCircle(sketch, "E162.MirrorC", {"center": v(93.5, 18.5) * mm, "radius": 0.5 * mm});
            skCircle(sketch, "E163.MirrorC", {"center": v(83.5, 18.5) * mm, "radius": 0.5 * mm});
            skCircle(sketch, "E164.MirrorC", {"center": v(143.5, 18.5) * mm, "radius": 0.5 * mm});
            skCircle(sketch, "E165.MirrorC", {"center": v(73.5, 18.5) * mm, "radius": 0.5 * mm});
            skCircle(sketch, "E166.MirrorC", {"center": v(133.5, 18.5) * mm, "radius": 0.5 * mm});
            skCircle(sketch, "E167.MirrorC", {"center": v(123.5, 18.5) * mm, "radius": 0.5 * mm});
            skCircle(sketch, "E168.MirrorC", {"center": v(113.5, 18.5) * mm, "radius": 0.5 * mm});
            skCircle(sketch, "E169.MirrorC", {"center": v(13.5, 4) * mm, "radius": 0.5 * mm});
            skCircle(sketch, "E170.MirrorC", {"center": v(153.5, 18.5) * mm, "radius": 0.5 * mm});
            skCircle(sketch, "E171.MirrorC", {"center": v(146, 6.5) * mm, "radius": 0.5 * mm});
            skCircle(sketch, "E172.MirrorC", {"center": v(26, 16) * mm, "radius": 0.5 * mm});
            skCircle(sketch, "E173.MirrorC", {"center": v(16, 16) * mm, "radius": 0.5 * mm});
            skCircle(sketch, "E174.MirrorC", {"center": v(66, 16) * mm, "radius": 0.5 * mm});
            skCircle(sketch, "E175.MirrorC", {"center": v(56, 16) * mm, "radius": 0.5 * mm});
            skCircle(sketch, "E176.MirrorC", {"center": v(46, 16) * mm, "radius": 0.5 * mm});
            skCircle(sketch, "E177.MirrorC", {"center": v(36, 16) * mm, "radius": 0.5 * mm});
            skCircle(sketch, "E178.MirrorC", {"center": v(106, 16) * mm, "radius": 0.5 * mm});
            skCircle(sketch, "E179.MirrorC", {"center": v(96, 16) * mm, "radius": 0.5 * mm});
            skCircle(sketch, "E180.MirrorC", {"center": v(86, 16) * mm, "radius": 0.5 * mm});
            skCircle(sketch, "E181.MirrorC", {"center": v(76, 16) * mm, "radius": 0.5 * mm});
            skCircle(sketch, "E182.MirrorC", {"center": v(146, 16) * mm, "radius": 0.5 * mm});
            skCircle(sketch, "E183.MirrorC", {"center": v(136, 16) * mm, "radius": 0.5 * mm});
            skCircle(sketch, "E184.MirrorC", {"center": v(126, 16) * mm, "radius": 0.5 * mm});
            skCircle(sketch, "E185.MirrorC", {"center": v(116, 16) * mm, "radius": 0.5 * mm});
            skCircle(sketch, "E186.MirrorC", {"center": v(61, 6.5) * mm, "radius": 0.5 * mm});
            skCircle(sketch, "E187.MirrorC", {"center": v(41, 6.5) * mm, "radius": 0.5 * mm});
            skCircle(sketch, "E188.MirrorC", {"center": v(16, 6.5) * mm, "radius": 0.5 * mm});
            skCircle(sketch, "E189.MirrorC", {"center": v(156, 16) * mm, "radius": 0.5 * mm});
            skCircle(sketch, "E190.MirrorC", {"center": v(26, 18.5) * mm, "radius": 0.5 * mm});
            skCircle(sketch, "E191.MirrorC", {"center": v(16, 18.5) * mm, "radius": 0.5 * mm});
            skCircle(sketch, "E192.MirrorC", {"center": v(66, 18.5) * mm, "radius": 0.5 * mm});
            skCircle(sketch, "E193.MirrorC", {"center": v(56, 18.5) * mm, "radius": 0.5 * mm});
            skCircle(sketch, "E194.MirrorC", {"center": v(46, 18.5) * mm, "radius": 0.5 * mm});
            skCircle(sketch, "E195.MirrorC", {"center": v(36, 18.5) * mm, "radius": 0.5 * mm});
            skCircle(sketch, "E196.MirrorC", {"center": v(106, 18.5) * mm, "radius": 0.5 * mm});
            skCircle(sketch, "E197.MirrorC", {"center": v(96, 18.5) * mm, "radius": 0.5 * mm});
            skCircle(sketch, "E198.MirrorC", {"center": v(86, 18.5) * mm, "radius": 0.5 * mm});
            skCircle(sketch, "E199.MirrorC", {"center": v(76, 18.5) * mm, "radius": 0.5 * mm});
            skCircle(sketch, "E200.MirrorC", {"center": v(146, 18.5) * mm, "radius": 0.5 * mm});
            skCircle(sketch, "E201.MirrorC", {"center": v(136, 18.5) * mm, "radius": 0.5 * mm});
            skCircle(sketch, "E202.MirrorC", {"center": v(126, 18.5) * mm, "radius": 0.5 * mm});
            skCircle(sketch, "E203.MirrorC", {"center": v(116, 18.5) * mm, "radius": 0.5 * mm});
            skCircle(sketch, "E204.MirrorC", {"center": v(63.5, 4) * mm, "radius": 0.5 * mm});
            skCircle(sketch, "E205.MirrorC", {"center": v(43.5, 6.5) * mm, "radius": 0.5 * mm});
            skCircle(sketch, "E206.MirrorC", {"center": v(18.5, 4) * mm, "radius": 0.5 * mm});
            skCircle(sketch, "E207.MirrorC", {"center": v(156, 18.5) * mm, "radius": 0.5 * mm});
            skCircle(sketch, "E208.MirrorC", {"center": v(151, 4) * mm, "radius": 0.5 * mm});
            skCircle(sketch, "E209.MirrorC", {"center": v(133.5, 4) * mm, "radius": 0.5 * mm});
            skCircle(sketch, "E210.MirrorC", {"center": v(46, 21) * mm, "radius": 0.5 * mm});
            skCircle(sketch, "E211.MirrorC", {"center": v(36, 21) * mm, "radius": 0.5 * mm});
            skCircle(sketch, "E212.MirrorC", {"center": v(26, 21) * mm, "radius": 0.5 * mm});
            skCircle(sketch, "E213.MirrorC", {"center": v(16, 21) * mm, "radius": 0.5 * mm});
            skCircle(sketch, "E214.MirrorC", {"center": v(86, 21) * mm, "radius": 0.5 * mm});
            skCircle(sketch, "E215.MirrorC", {"center": v(76, 21) * mm, "radius": 0.5 * mm});
            skCircle(sketch, "E216.MirrorC", {"center": v(66, 21) * mm, "radius": 0.5 * mm});
            skCircle(sketch, "E217.MirrorC", {"center": v(56, 21) * mm, "radius": 0.5 * mm});
            skCircle(sketch, "E218.MirrorC", {"center": v(126, 21) * mm, "radius": 0.5 * mm});
            skCircle(sketch, "E219.MirrorC", {"center": v(116, 21) * mm, "radius": 0.5 * mm});
            skCircle(sketch, "E220.MirrorC", {"center": v(106, 21) * mm, "radius": 0.5 * mm});
            skCircle(sketch, "E221.MirrorC", {"center": v(96, 21) * mm, "radius": 0.5 * mm});
            skCircle(sketch, "E222.MirrorC", {"center": v(18.5, 6.5) * mm, "radius": 0.5 * mm});
            skCircle(sketch, "E223.MirrorC", {"center": v(156, 21) * mm, "radius": 0.5 * mm});
            skCircle(sketch, "E224.MirrorC", {"center": v(146, 21) * mm, "radius": 0.5 * mm});
            skCircle(sketch, "E225.MirrorC", {"center": v(136, 21) * mm, "radius": 0.5 * mm});
            skCircle(sketch, "E226.MirrorC", {"center": v(63.5, 6.5) * mm, "radius": 0.5 * mm});
            skCircle(sketch, "E227.MirrorC", {"center": v(151, 6.5) * mm, "radius": 0.5 * mm});
            skCircle(sketch, "E228.MirrorC", {"center": v(131, 6.5) * mm, "radius": 0.5 * mm});
            skCircle(sketch, "E229.MirrorC", {"center": v(48.5, 13.5) * mm, "radius": 0.5 * mm});
            skCircle(sketch, "E230.MirrorC", {"center": v(38.5, 13.5) * mm, "radius": 0.5 * mm});
            skCircle(sketch, "E231.MirrorC", {"center": v(28.5, 13.5) * mm, "radius": 0.5 * mm});
            skCircle(sketch, "E232.MirrorC", {"center": v(18.5, 13.5) * mm, "radius": 0.5 * mm});
            skCircle(sketch, "E233.MirrorC", {"center": v(88.5, 13.5) * mm, "radius": 0.5 * mm});
            skCircle(sketch, "E234.MirrorC", {"center": v(78.5, 13.5) * mm, "radius": 0.5 * mm});
            skCircle(sketch, "E235.MirrorC", {"center": v(68.5, 13.5) * mm, "radius": 0.5 * mm});
            skCircle(sketch, "E236.MirrorC", {"center": v(58.5, 13.5) * mm, "radius": 0.5 * mm});
            skCircle(sketch, "E237.MirrorC", {"center": v(128.5, 13.5) * mm, "radius": 0.5 * mm});
            skCircle(sketch, "E238.MirrorC", {"center": v(118.5, 13.5) * mm, "radius": 0.5 * mm});
            skCircle(sketch, "E239.MirrorC", {"center": v(108.5, 13.5) * mm, "radius": 0.5 * mm});
            skCircle(sketch, "E240.MirrorC", {"center": v(98.5, 13.5) * mm, "radius": 0.5 * mm});
            skCircle(sketch, "E241.MirrorC", {"center": v(158.5, 13.5) * mm, "radius": 0.5 * mm});
            skCircle(sketch, "E242.MirrorC", {"center": v(148.5, 13.5) * mm, "radius": 0.5 * mm});
            skCircle(sketch, "E243.MirrorC", {"center": v(138.5, 13.5) * mm, "radius": 0.5 * mm});
            skCircle(sketch, "E244.MirrorC", {"center": v(153.5, 4) * mm, "radius": 0.5 * mm});
            skCircle(sketch, "E245.MirrorC", {"center": v(133.5, 6.5) * mm, "radius": 0.5 * mm});
            skCircle(sketch, "E246.MirrorC", {"center": v(78.5, 6.5) * mm, "radius": 0.5 * mm});
            skCircle(sketch, "E247.MirrorC", {"center": v(48.5, 16) * mm, "radius": 0.5 * mm});
            skCircle(sketch, "E248.MirrorC", {"center": v(28.5, 16) * mm, "radius": 0.5 * mm});
            skCircle(sketch, "E249.MirrorC", {"center": v(38.5, 16) * mm, "radius": 0.5 * mm});
            skCircle(sketch, "E250.MirrorC", {"center": v(18.5, 16) * mm, "radius": 0.5 * mm});
            skCircle(sketch, "E251.MirrorC", {"center": v(88.5, 16) * mm, "radius": 0.5 * mm});
            skCircle(sketch, "E252.MirrorC", {"center": v(78.5, 16) * mm, "radius": 0.5 * mm});
            skCircle(sketch, "E253.MirrorC", {"center": v(68.5, 16) * mm, "radius": 0.5 * mm});
            skCircle(sketch, "E254.MirrorC", {"center": v(58.5, 16) * mm, "radius": 0.5 * mm});
            skCircle(sketch, "E255.MirrorC", {"center": v(128.5, 16) * mm, "radius": 0.5 * mm});
            skCircle(sketch, "E256.MirrorC", {"center": v(118.5, 16) * mm, "radius": 0.5 * mm});
            skCircle(sketch, "E257.MirrorC", {"center": v(108.5, 16) * mm, "radius": 0.5 * mm});
            skCircle(sketch, "E258.MirrorC", {"center": v(98.5, 16) * mm, "radius": 0.5 * mm});
            skCircle(sketch, "E259.MirrorC", {"center": v(28.5, 4) * mm, "radius": 0.5 * mm});
            skCircle(sketch, "E260.MirrorC", {"center": v(23.5, 18.5) * mm, "radius": 0.5 * mm});
            skCircle(sketch, "E261.MirrorC", {"center": v(158.5, 16) * mm, "radius": 0.5 * mm});
            skCircle(sketch, "E262.MirrorC", {"center": v(138.5, 16) * mm, "radius": 0.5 * mm});
            skCircle(sketch, "E263.MirrorC", {"center": v(148.5, 16) * mm, "radius": 0.5 * mm});
            skCircle(sketch, "E264.MirrorC", {"center": v(13.5, 18.5) * mm, "radius": 0.5 * mm});
            skCircle(sketch, "E265.MirrorC", {"center": v(63.5, 18.5) * mm, "radius": 0.5 * mm});
            skCircle(sketch, "E266.MirrorC", {"center": v(53.5, 18.5) * mm, "radius": 0.5 * mm});
            skCircle(sketch, "E267.MirrorC", {"center": v(43.5, 18.5) * mm, "radius": 0.5 * mm});
            skCircle(sketch, "E268.MirrorC", {"center": v(53.5, 6.5) * mm, "radius": 0.5 * mm});
            skCircle(sketch, "E269.MirrorC", {"center": v(46, 4) * mm, "radius": 0.5 * mm});
            skCircle(sketch, "E270.MirrorC", {"center": v(153.5, 6.5) * mm, "radius": 0.5 * mm});
            skCircle(sketch, "E271.MirrorC", {"center": v(48.5, 18.5) * mm, "radius": 0.5 * mm});
            skCircle(sketch, "E272.MirrorC", {"center": v(38.5, 18.5) * mm, "radius": 0.5 * mm});
            skCircle(sketch, "E273.MirrorC", {"center": v(28.5, 18.5) * mm, "radius": 0.5 * mm});
            skCircle(sketch, "E274.MirrorC", {"center": v(18.5, 18.5) * mm, "radius": 0.5 * mm});
            skCircle(sketch, "E275.MirrorC", {"center": v(88.5, 18.5) * mm, "radius": 0.5 * mm});
            skCircle(sketch, "E276.MirrorC", {"center": v(78.5, 18.5) * mm, "radius": 0.5 * mm});
            skCircle(sketch, "E277.MirrorC", {"center": v(58.5, 18.5) * mm, "radius": 0.5 * mm});
            skCircle(sketch, "E278.MirrorC", {"center": v(68.5, 18.5) * mm, "radius": 0.5 * mm});
            skCircle(sketch, "E279.MirrorC", {"center": v(118.5, 18.5) * mm, "radius": 0.5 * mm});
            skCircle(sketch, "E280.MirrorC", {"center": v(128.5, 18.5) * mm, "radius": 0.5 * mm});
            skCircle(sketch, "E281.MirrorC", {"center": v(98.5, 18.5) * mm, "radius": 0.5 * mm});
            skCircle(sketch, "E282.MirrorC", {"center": v(108.5, 18.5) * mm, "radius": 0.5 * mm});
            skCircle(sketch, "E283.MirrorC", {"center": v(33.5, 18.5) * mm, "radius": 0.5 * mm});
            skCircle(sketch, "E284.MirrorC", {"center": v(61, 4) * mm, "radius": 0.5 * mm});
            skCircle(sketch, "E285.MirrorC", {"center": v(43.5, 4) * mm, "radius": 0.5 * mm});
            skCircle(sketch, "E286.MirrorC", {"center": v(48.5, 6.5) * mm, "radius": 0.5 * mm});
            skCircle(sketch, "E287.MirrorC", {"center": v(73.5, 6.5) * mm, "radius": 0.5 * mm});
            skCircle(sketch, "E288.MirrorC", {"center": v(141, 13.5) * mm, "radius": 0.5 * mm});
            skCircle(sketch, "E289.MirrorC", {"center": v(151, 13.5) * mm, "radius": 0.5 * mm});
            skCircle(sketch, "E290.MirrorC", {"center": v(101, 13.5) * mm, "radius": 0.5 * mm});
            skCircle(sketch, "E291.MirrorC", {"center": v(111, 13.5) * mm, "radius": 0.5 * mm});
            skCircle(sketch, "E292.MirrorC", {"center": v(73.5, 21) * mm, "radius": 0.5 * mm});
            skCircle(sketch, "E293.MirrorC", {"center": v(121, 13.5) * mm, "radius": 0.5 * mm});
            skCircle(sketch, "E294.MirrorC", {"center": v(83.5, 21) * mm, "radius": 0.5 * mm});
            skCircle(sketch, "E295.MirrorC", {"center": v(131, 13.5) * mm, "radius": 0.5 * mm});
            skCircle(sketch, "E296.MirrorC", {"center": v(61, 13.5) * mm, "radius": 0.5 * mm});
            skCircle(sketch, "E297.MirrorC", {"center": v(71, 13.5) * mm, "radius": 0.5 * mm});
            skCircle(sketch, "E298.MirrorC", {"center": v(93.5, 21) * mm, "radius": 0.5 * mm});
            skCircle(sketch, "E299.MirrorC", {"center": v(81, 13.5) * mm, "radius": 0.5 * mm});
            skCircle(sketch, "E300.MirrorC", {"center": v(91, 13.5) * mm, "radius": 0.5 * mm});
            skCircle(sketch, "E301.MirrorC", {"center": v(21, 13.5) * mm, "radius": 0.5 * mm});
            skCircle(sketch, "E302.MirrorC", {"center": v(31, 13.5) * mm, "radius": 0.5 * mm});
            skCircle(sketch, "E303.MirrorC", {"center": v(51, 13.5) * mm, "radius": 0.5 * mm});
            skCircle(sketch, "E304.MirrorC", {"center": v(41, 13.5) * mm, "radius": 0.5 * mm});
            skCircle(sketch, "E305.MirrorC", {"center": v(136, 4) * mm, "radius": 0.5 * mm});
            skCircle(sketch, "E306.MirrorC", {"center": v(143.5, 6.5) * mm, "radius": 0.5 * mm});
            skCircle(sketch, "E307.MirrorC", {"center": v(48.5, 4) * mm, "radius": 0.5 * mm});
            skCircle(sketch, "E308.MirrorC", {"center": v(71, 6.5) * mm, "radius": 0.5 * mm});
            skCircle(sketch, "E309.MirrorC", {"center": v(103.5, 21) * mm, "radius": 0.5 * mm});
            skCircle(sketch, "E310.MirrorC", {"center": v(33.5, 21) * mm, "radius": 0.5 * mm});
            skCircle(sketch, "E311.MirrorC", {"center": v(43.5, 21) * mm, "radius": 0.5 * mm});
            skCircle(sketch, "E312.MirrorC", {"center": v(53.5, 21) * mm, "radius": 0.5 * mm});
            skCircle(sketch, "E313.MirrorC", {"center": v(63.5, 21) * mm, "radius": 0.5 * mm});
            skCircle(sketch, "E314.MirrorC", {"center": v(13.5, 21) * mm, "radius": 0.5 * mm});
            skCircle(sketch, "E315.MirrorC", {"center": v(23.5, 21) * mm, "radius": 0.5 * mm});
            skCircle(sketch, "E316.MirrorC", {"center": v(138.5, 21) * mm, "radius": 0.5 * mm});
            skCircle(sketch, "E317.MirrorC", {"center": v(158.5, 21) * mm, "radius": 0.5 * mm});
            skCircle(sketch, "E318.MirrorC", {"center": v(28.5, 6.5) * mm, "radius": 0.5 * mm});
            skCircle(sketch, "E319.MirrorC", {"center": v(148.5, 21) * mm, "radius": 0.5 * mm});
            skCircle(sketch, "E320.MirrorC", {"center": v(98.5, 21) * mm, "radius": 0.5 * mm});
            skCircle(sketch, "E321.MirrorC", {"center": v(118.5, 21) * mm, "radius": 0.5 * mm});
            skCircle(sketch, "E322.MirrorC", {"center": v(108.5, 21) * mm, "radius": 0.5 * mm});
            skCircle(sketch, "E323.MirrorC", {"center": v(58.5, 21) * mm, "radius": 0.5 * mm});
            skCircle(sketch, "E324.MirrorC", {"center": v(128.5, 21) * mm, "radius": 0.5 * mm});
            skCircle(sketch, "E325.MirrorC", {"center": v(68.5, 21) * mm, "radius": 0.5 * mm});
            skCircle(sketch, "E326.MirrorC", {"center": v(78.5, 21) * mm, "radius": 0.5 * mm});
            skCircle(sketch, "E327.MirrorC", {"center": v(88.5, 21) * mm, "radius": 0.5 * mm});
            skCircle(sketch, "E328.MirrorC", {"center": v(28.5, 21) * mm, "radius": 0.5 * mm});
            skCircle(sketch, "E329.MirrorC", {"center": v(18.5, 21) * mm, "radius": 0.5 * mm});
            skCircle(sketch, "E330.MirrorC", {"center": v(38.5, 21) * mm, "radius": 0.5 * mm});
            skCircle(sketch, "E331.MirrorC", {"center": v(48.5, 21) * mm, "radius": 0.5 * mm});
            skCircle(sketch, "E332.MirrorC", {"center": v(153.5, 21) * mm, "radius": 0.5 * mm});
            skCircle(sketch, "E333.MirrorC", {"center": v(148.5, 6.5) * mm, "radius": 0.5 * mm});
            skCircle(sketch, "E334.MirrorC", {"center": v(73.5, 4) * mm, "radius": 0.5 * mm});
            skCircle(sketch, "E335.MirrorC", {"center": v(46, 6.5) * mm, "radius": 0.5 * mm});
            skCircle(sketch, "E336.MirrorC", {"center": v(13.5, 6.5) * mm, "radius": 0.5 * mm});
            skCircle(sketch, "E337.MirrorC", {"center": v(148.5, 18.5) * mm, "radius": 0.5 * mm});
            skCircle(sketch, "E338.MirrorC", {"center": v(138.5, 18.5) * mm, "radius": 0.5 * mm});
            skCircle(sketch, "E339.MirrorC", {"center": v(26, 6.5) * mm, "radius": 0.5 * mm});
            skCircle(sketch, "E340.MirrorC", {"center": v(158.5, 18.5) * mm, "radius": 0.5 * mm});
            skCircle(sketch, "E341.MirrorC", {"center": v(113.5, 21) * mm, "radius": 0.5 * mm});
            skCircle(sketch, "E342.MirrorC", {"center": v(123.5, 21) * mm, "radius": 0.5 * mm});
            skCircle(sketch, "E343.MirrorC", {"center": v(133.5, 21) * mm, "radius": 0.5 * mm});
            skCircle(sketch, "E344.MirrorC", {"center": v(143.5, 21) * mm, "radius": 0.5 * mm});
            skLineSegment(sketch, "E345.MirrorCS", {"start": v(8.5, 6.5) * mm, "end": v(23.5, 6.5) * mm, "construction": true});
            skCircle(sketch, "E346.MirrorC", {"center": v(116, 4) * mm, "radius": 0.5 * mm});
            skCircle(sketch, "E347.MirrorC", {"center": v(113.5, 4) * mm, "radius": 0.5 * mm});
            skLineSegment(sketch, "E348.MirrorCS", {"start": v(98.5, 4) * mm, "end": v(101, 4) * mm, "construction": true});
            skLineSegment(sketch, "E349.MirrorCS", {"start": v(113.5, 4) * mm, "end": v(116, 4) * mm, "construction": true});
            skCircle(sketch, "E350.MirrorC", {"center": v(98.5, 4) * mm, "radius": 0.5 * mm});
            skCircle(sketch, "E351.MirrorC", {"center": v(86, 4) * mm, "radius": 0.5 * mm});
            skCircle(sketch, "E352.MirrorC", {"center": v(101, 4) * mm, "radius": 0.5 * mm});
            skCircle(sketch, "E353.MirrorC", {"center": v(93.5, 6.5) * mm, "radius": 0.5 * mm});
            skCircle(sketch, "E354.MirrorC", {"center": v(118.5, 6.5) * mm, "radius": 0.5 * mm});
            skCircle(sketch, "E355.MirrorC", {"center": v(121, 4) * mm, "radius": 0.5 * mm});
            skCircle(sketch, "E356.MirrorC", {"center": v(103.5, 4) * mm, "radius": 0.5 * mm});
            skCircle(sketch, "E357.MirrorC", {"center": v(121, 6.5) * mm, "radius": 0.5 * mm});
            skCircle(sketch, "E358.MirrorC", {"center": v(101, 6.5) * mm, "radius": 0.5 * mm});
            skCircle(sketch, "E359.MirrorC", {"center": v(113.5, 6.5) * mm, "radius": 0.5 * mm});
            skCircle(sketch, "E360.MirrorC", {"center": v(106, 4) * mm, "radius": 0.5 * mm});
            skCircle(sketch, "E361.MirrorC", {"center": v(88.5, 4) * mm, "radius": 0.5 * mm});
            skCircle(sketch, "E362.MirrorC", {"center": v(123.5, 4) * mm, "radius": 0.5 * mm});
            skCircle(sketch, "E363.MirrorC", {"center": v(103.5, 6.5) * mm, "radius": 0.5 * mm});
            skCircle(sketch, "E364.MirrorC", {"center": v(106, 6.5) * mm, "radius": 0.5 * mm});
            skCircle(sketch, "E365.MirrorC", {"center": v(86, 6.5) * mm, "radius": 0.5 * mm});
            skCircle(sketch, "E366.MirrorC", {"center": v(108.5, 4) * mm, "radius": 0.5 * mm});
            skCircle(sketch, "E367.MirrorC", {"center": v(88.5, 6.5) * mm, "radius": 0.5 * mm});
            skCircle(sketch, "E368.MirrorC", {"center": v(108.5, 6.5) * mm, "radius": 0.5 * mm});
            skCircle(sketch, "E369.MirrorC", {"center": v(93.5, 4) * mm, "radius": 0.5 * mm});
            skCircle(sketch, "E370.MirrorC", {"center": v(116, 6.5) * mm, "radius": 0.5 * mm});
            skCircle(sketch, "E371.MirrorC", {"center": v(91, 6.5) * mm, "radius": 0.5 * mm});
            skCircle(sketch, "E372.MirrorC", {"center": v(118.5, 4) * mm, "radius": 0.5 * mm});
            skCircle(sketch, "E373.MirrorC", {"center": v(123.5, 6.5) * mm, "radius": 0.5 * mm});
            skCircle(sketch, "E374.MirrorC", {"center": v(98.5, 6.5) * mm, "radius": 0.5 * mm});
            skCircle(sketch, "E375.MirrorC", {"center": v(91, 4) * mm, "radius": 0.5 * mm});
            skSolve(sketch);
        }
        {
            var Q0;
            Q0 = qSketchRegion(id + "F4", true);
            extrude(context, id + "F5", {"entities" : qUnion([Q0]), "operationType" : NewBodyOperationType.REMOVE, "oppositeDirection" : true, "depth" : 7.75 * mm, "offsetDistance" : 25 * mm});
        }
        {
            var Q0;
            Q0=makeQuery(id+"F1.opExtrude","SWEPT_FACE",FACE,{"disambiguationData":[OSD([sQuery(id+"F0.wireOp",EDGE,"E0.bottom")])]});
            var sketch = newSketch(context, id + "F6", { "sketchPlane" : qUnion([Q0])});
            skLineSegment(sketch, "E376.bottom", {"start": v(12.5, 5.65) * mm, "end": v(16.6, 5.65) * mm});
            skLineSegment(sketch, "E376.top", {"start": v(12.5, 0.65) * mm, "end": v(16.6, 0.65) * mm});
            skLineSegment(sketch, "E376.left", {"start": v(12.5, 5.65) * mm, "end": v(12.5, 0.65) * mm});
            skLineSegment(sketch, "E376.right", {"start": v(16.6, 5.65) * mm, "end": v(16.6, 0.65) * mm});
            skLineSegment(sketch, "E377.1.0.0", {"start": v(80, 5.65) * mm, "end": v(84.1, 5.65) * mm});
            skLineSegment(sketch, "E377.1.0.1", {"start": v(80, 0.65) * mm, "end": v(84.1, 0.65) * mm});
            skLineSegment(sketch, "E377.1.0.2", {"start": v(80, 5.65) * mm, "end": v(80, 0.65) * mm});
            skLineSegment(sketch, "E377.1.0.3", {"start": v(84.1, 5.65) * mm, "end": v(84.1, 0.65) * mm});
            skLineSegment(sketch, "E377.2.0.0", {"start": v(147.5, 5.65) * mm, "end": v(151.6, 5.65) * mm});
            skLineSegment(sketch, "E377.2.0.1", {"start": v(147.5, 0.65) * mm, "end": v(151.6, 0.65) * mm});
            skLineSegment(sketch, "E377.2.0.2", {"start": v(147.5, 5.65) * mm, "end": v(147.5, 0.65) * mm});
            skLineSegment(sketch, "E377.2.0.3", {"start": v(151.6, 5.65) * mm, "end": v(151.6, 0.65) * mm});
            skLineSegment(sketch, "E377.direction1", {"start": v(12.5, 0.65) * mm, "end": v(80, 0.65) * mm, "construction": true});
            skSolve(sketch);
        }
        {
            var Q0;
            Q0 = qSketchRegion(id + "F6", true);
            extrude(context, id + "F7", {"entities" : qUnion([Q0]), "operationType" : NewBodyOperationType.ADD, "depth" : 1.5 * mm, "offsetDistance" : 25 * mm});
        }
        {
            var Q0;
            Q0=makeQuery(id+"F7.opExtrude","SWEPT_FACE",FACE,{"disambiguationData":[OSD([sQuery(id+"F6.wireOp",EDGE,"E376.bottom")])]});
            var sketch = newSketch(context, id + "F8", { "sketchPlane" : qUnion([Q0])});
            skLineSegment(sketch, "E378", {"start": v(12.5, -1.5) * mm, "end": v(12.5, 0) * mm});
            skLineSegment(sketch, "E379", {"start": v(12.5, 0) * mm, "end": v(12.9, 0) * mm});
            skLineSegment(sketch, "E380", {"start": v(12.9, 0) * mm, "end": v(12.5, -1.5) * mm});
            skLineSegment(sketch, "E381", {"start": v(14.55, -2.85) * mm, "end": v(14.55, 0.52) * mm, "construction": true});
            skPoint(sketch, "E381.startSnap0", {"position": v(14.55, -1.5) * mm});
            skPoint(sketch, "E381.endSnap0", {"position": v(14.55, 0) * mm});
            skLineSegment(sketch, "E382.MirrorCS", {"start": v(16.6, -1.5) * mm, "end": v(16.6, 0) * mm});
            skLineSegment(sketch, "E383.MirrorCS", {"start": v(16.2, 0) * mm, "end": v(16.6, -1.5) * mm});
            skLineSegment(sketch, "E384.MirrorCS", {"start": v(16.6, 0) * mm, "end": v(16.2, 0) * mm});
            skLineSegment(sketch, "E385.1.0.0", {"start": v(80, -1.5) * mm, "end": v(80, 0) * mm});
            skLineSegment(sketch, "E385.1.0.1", {"start": v(80.4, 0) * mm, "end": v(80, -1.5) * mm});
            skLineSegment(sketch, "E385.1.0.2", {"start": v(80, 0) * mm, "end": v(80.4, 0) * mm});
            skLineSegment(sketch, "E385.1.0.3", {"start": v(84.1, -1.5) * mm, "end": v(84.1, 0) * mm});
            skLineSegment(sketch, "E385.1.0.4", {"start": v(83.7, 0) * mm, "end": v(84.1, -1.5) * mm});
            skLineSegment(sketch, "E385.1.0.5", {"start": v(84.1, 0) * mm, "end": v(83.7, 0) * mm});
            skLineSegment(sketch, "E385.2.0.0", {"start": v(147.5, -1.5) * mm, "end": v(147.5, 0) * mm});
            skLineSegment(sketch, "E385.2.0.1", {"start": v(147.9, 0) * mm, "end": v(147.5, -1.5) * mm});
            skLineSegment(sketch, "E385.2.0.2", {"start": v(147.5, 0) * mm, "end": v(147.9, 0) * mm});
            skLineSegment(sketch, "E385.2.0.3", {"start": v(151.6, -1.5) * mm, "end": v(151.6, 0) * mm});
            skLineSegment(sketch, "E385.2.0.4", {"start": v(151.2, 0) * mm, "end": v(151.6, -1.5) * mm});
            skLineSegment(sketch, "E385.2.0.5", {"start": v(151.6, 0) * mm, "end": v(151.2, 0) * mm});
            skLineSegment(sketch, "E385.direction1", {"start": v(12.5, -1.5) * mm, "end": v(80, -1.5) * mm, "construction": true});
            skSolve(sketch);
        }
        {
            var Q0;
            Q0 = qSketchRegion(id + "F8", true);
            extrude(context, id + "F9", {"entities" : qUnion([Q0]), "operationType" : NewBodyOperationType.REMOVE, "endBound" : BoundingType.UP_TO_NEXT, "oppositeDirection" : true, "depth" : 25 * mm, "offsetDistance" : 25 * mm});
        }
        {
            var Q0;
            Q0=makeQuery(id+"F1.opExtrude","CAP_FACE",FACE,{"disambiguationData":[OSD([sQuery(id+"F0.wireOp",EDGE,"E0.bottom"),sQuery(id+"F0.wireOp",EDGE,"E0.top"),sQuery(id+"F0.wireOp",EDGE,"E0.left"),sQuery(id+"F0.wireOp",EDGE,"E0.right")])],"isStart":true});
            var sketch = newSketch(context, id + "F10", { "sketchPlane" : qUnion([Q0])});
            skLineSegment(sketch, "E386", {"start": v(12.9, -54) * mm, "end": v(12.5, -52.5) * mm});
            skLineSegment(sketch, "E387", {"start": v(12.5, -52.5) * mm, "end": v(16.6, -52.5) * mm});
            skLineSegment(sketch, "E388", {"start": v(16.6, -52.5) * mm, "end": v(16.2, -54) * mm});
            skLineSegment(sketch, "E389", {"start": v(12.9, -54) * mm, "end": v(16.2, -54) * mm});
            skLineSegment(sketch, "E390.1.0.0", {"start": v(80.4, -54) * mm, "end": v(83.7, -54) * mm});
            skLineSegment(sketch, "E390.1.0.1", {"start": v(84.1, -52.5) * mm, "end": v(83.7, -54) * mm});
            skLineSegment(sketch, "E390.1.0.2", {"start": v(80, -52.5) * mm, "end": v(84.1, -52.5) * mm});
            skLineSegment(sketch, "E390.1.0.3", {"start": v(80.4, -54) * mm, "end": v(80, -52.5) * mm});
            skLineSegment(sketch, "E390.2.0.0", {"start": v(147.9, -54) * mm, "end": v(151.2, -54) * mm});
            skLineSegment(sketch, "E390.2.0.1", {"start": v(151.6, -52.5) * mm, "end": v(151.2, -54) * mm});
            skLineSegment(sketch, "E390.2.0.2", {"start": v(147.5, -52.5) * mm, "end": v(151.6, -52.5) * mm});
            skLineSegment(sketch, "E390.2.0.3", {"start": v(147.9, -54) * mm, "end": v(147.5, -52.5) * mm});
            skLineSegment(sketch, "E390.direction1", {"start": v(12.9, -54) * mm, "end": v(80.4, -54) * mm, "construction": true});
            skSolve(sketch);
        }
        {
            var Q0;
            Q0 = qSketchRegion(id + "F10", true);
            extrude(context, id + "F11", {"entities" : qUnion([Q0]), "operationType" : NewBodyOperationType.REMOVE, "oppositeDirection" : true, "depth" : 5.65 * mm, "offsetDistance" : 25 * mm});
        }
    });
